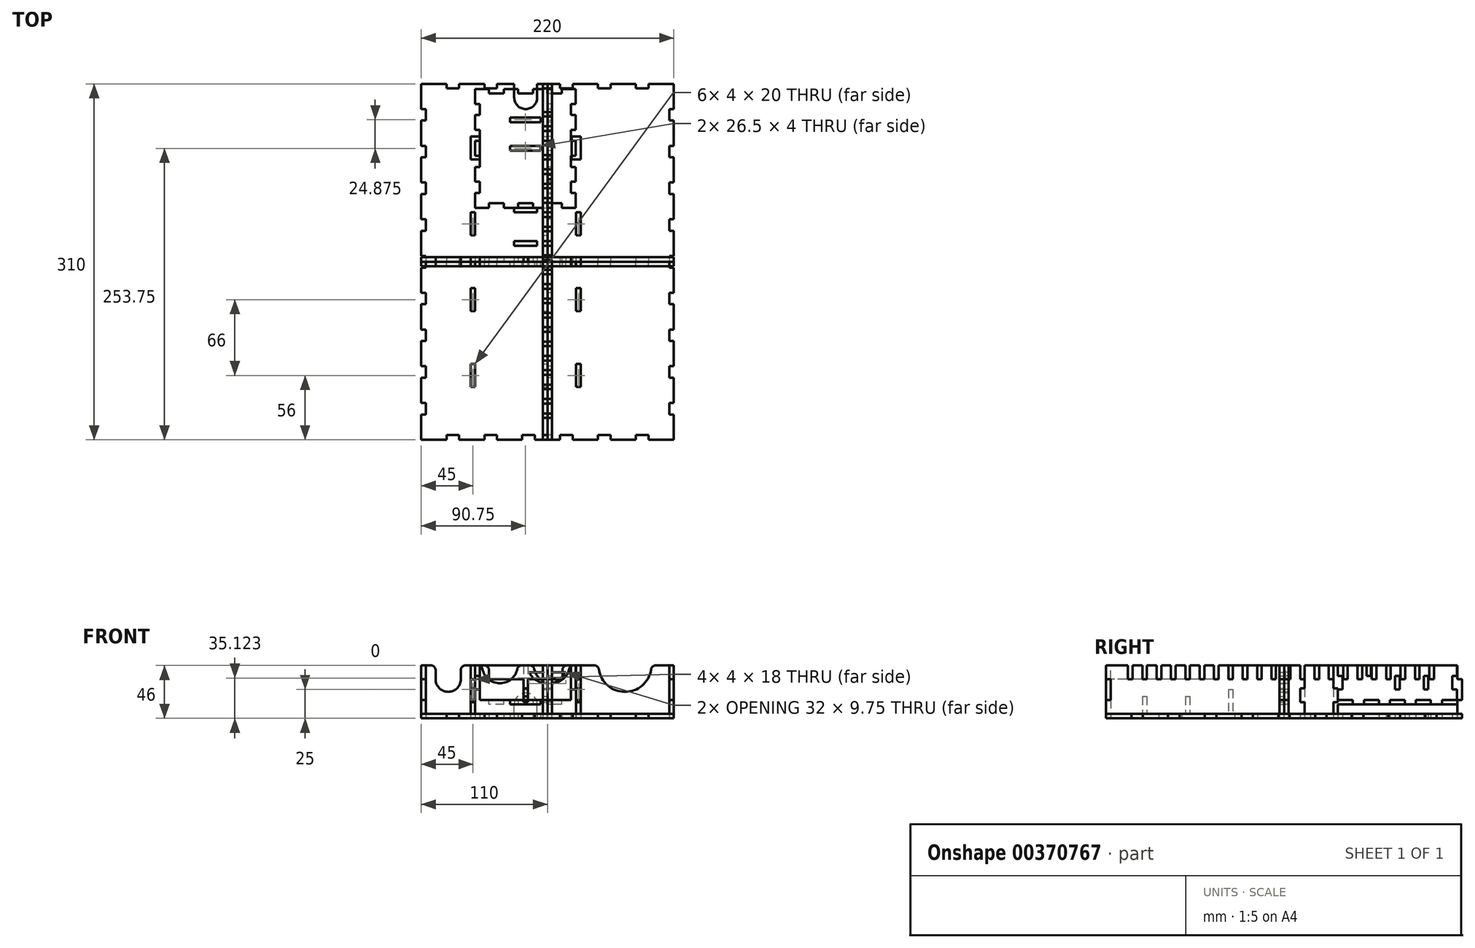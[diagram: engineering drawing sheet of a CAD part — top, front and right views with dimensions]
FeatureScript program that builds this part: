
annotation { "Feature Type Name" : "Feature", "Feature Type Description" : "" }
export const myFeature = defineFeature(function(context is Context, id is Id, definition is map)
    precondition{}
    {
        {
            assignVariable(context, id + "F0", {"name" : "thickness", "anyValue" : 4});
        }
        {
            var Q0;
            Q0=qCreatedBy(makeId("Top.planeOp"),FACE);
            var sketch = newSketch(context, id + "F1", { "sketchPlane" : qUnion([Q0])});
            skLineSegment(sketch, "E0", {"start": v(-110, 155) * mm, "end": v(-110, 133) * mm});
            skLineSegment(sketch, "E1", {"start": v(-110, 133) * mm, "end": v(-106, 133) * mm});
            skLineSegment(sketch, "E2", {"start": v(-106, 133) * mm, "end": v(-106, 123) * mm});
            skLineSegment(sketch, "E3", {"start": v(-106, 123) * mm, "end": v(-110, 123) * mm});
            skLineSegment(sketch, "E4.0.1.0", {"start": v(-106, 91) * mm, "end": v(-110, 91) * mm});
            skLineSegment(sketch, "E4.0.1.1", {"start": v(-110, 123) * mm, "end": v(-110, 101) * mm});
            skLineSegment(sketch, "E4.0.1.2", {"start": v(-106, 101) * mm, "end": v(-106, 91) * mm});
            skLineSegment(sketch, "E4.0.1.3", {"start": v(-110, 101) * mm, "end": v(-106, 101) * mm});
            skLineSegment(sketch, "E4.0.2.0", {"start": v(-106, 59) * mm, "end": v(-110, 59) * mm});
            skLineSegment(sketch, "E4.0.2.1", {"start": v(-110, 91) * mm, "end": v(-110, 69) * mm});
            skLineSegment(sketch, "E4.0.2.2", {"start": v(-106, 69) * mm, "end": v(-106, 59) * mm});
            skLineSegment(sketch, "E4.0.2.3", {"start": v(-110, 69) * mm, "end": v(-106, 69) * mm});
            skLineSegment(sketch, "E4.0.3.0", {"start": v(-106, 27) * mm, "end": v(-110, 27) * mm});
            skLineSegment(sketch, "E4.0.3.1", {"start": v(-110, 59) * mm, "end": v(-110, 37) * mm});
            skLineSegment(sketch, "E4.0.3.2", {"start": v(-106, 37) * mm, "end": v(-106, 27) * mm});
            skLineSegment(sketch, "E4.0.3.3", {"start": v(-110, 37) * mm, "end": v(-106, 37) * mm});
            skLineSegment(sketch, "E4.0.4.0", {"start": v(-106, -5) * mm, "end": v(-110, -5) * mm});
            skLineSegment(sketch, "E4.0.4.1", {"start": v(-110, 27) * mm, "end": v(-110, 5) * mm});
            skLineSegment(sketch, "E4.0.4.2", {"start": v(-106, 5) * mm, "end": v(-106, -5) * mm});
            skLineSegment(sketch, "E4.0.4.3", {"start": v(-110, 5) * mm, "end": v(-106, 5) * mm});
            skLineSegment(sketch, "E4.0.5.0", {"start": v(-106, -37) * mm, "end": v(-110, -37) * mm});
            skLineSegment(sketch, "E4.0.5.1", {"start": v(-110, -5) * mm, "end": v(-110, -27) * mm});
            skLineSegment(sketch, "E4.0.5.2", {"start": v(-106, -27) * mm, "end": v(-106, -37) * mm});
            skLineSegment(sketch, "E4.0.5.3", {"start": v(-110, -27) * mm, "end": v(-106, -27) * mm});
            skLineSegment(sketch, "E4.0.6.0", {"start": v(-106, -69) * mm, "end": v(-110, -69) * mm});
            skLineSegment(sketch, "E4.0.6.1", {"start": v(-110, -37) * mm, "end": v(-110, -59) * mm});
            skLineSegment(sketch, "E4.0.6.2", {"start": v(-106, -59) * mm, "end": v(-106, -69) * mm});
            skLineSegment(sketch, "E4.0.6.3", {"start": v(-110, -59) * mm, "end": v(-106, -59) * mm});
            skLineSegment(sketch, "E4.0.7.0", {"start": v(-106, -101) * mm, "end": v(-110, -101) * mm});
            skLineSegment(sketch, "E4.0.7.1", {"start": v(-110, -69) * mm, "end": v(-110, -91) * mm});
            skLineSegment(sketch, "E4.0.7.2", {"start": v(-106, -91) * mm, "end": v(-106, -101) * mm});
            skLineSegment(sketch, "E4.0.7.3", {"start": v(-110, -91) * mm, "end": v(-106, -91) * mm});
            skLineSegment(sketch, "E4.0.8.0", {"start": v(-106, -133) * mm, "end": v(-110, -133) * mm});
            skLineSegment(sketch, "E4.0.8.1", {"start": v(-110, -101) * mm, "end": v(-110, -123) * mm});
            skLineSegment(sketch, "E4.0.8.2", {"start": v(-106, -123) * mm, "end": v(-106, -133) * mm});
            skLineSegment(sketch, "E4.0.8.3", {"start": v(-110, -123) * mm, "end": v(-106, -123) * mm});
            skLineSegment(sketch, "E4.0.9.1", {"start": v(-110, -133) * mm, "end": v(-110, -155) * mm});
            skLineSegment(sketch, "E5", {"start": v(-110, 155) * mm, "end": v(-88, 155) * mm});
            skLineSegment(sketch, "E6", {"start": v(-88, 155) * mm, "end": v(-88, 151) * mm});
            skLineSegment(sketch, "E7", {"start": v(-88, 151) * mm, "end": v(-77, 151) * mm});
            skLineSegment(sketch, "E8", {"start": v(-77, 151) * mm, "end": v(-77, 155) * mm});
            skLineSegment(sketch, "E9.1.0.0", {"start": v(-44, 151) * mm, "end": v(-44, 155) * mm});
            skLineSegment(sketch, "E9.1.0.1", {"start": v(-55, 151) * mm, "end": v(-44, 151) * mm});
            skLineSegment(sketch, "E9.1.0.2", {"start": v(-77, 155) * mm, "end": v(-55, 155) * mm});
            skLineSegment(sketch, "E9.1.0.3", {"start": v(-55, 155) * mm, "end": v(-55, 151) * mm});
            skLineSegment(sketch, "E9.2.0.0", {"start": v(-11, 151) * mm, "end": v(-11, 155) * mm, "construction": true});
            skLineSegment(sketch, "E9.2.0.1", {"start": v(-22, 151) * mm, "end": v(-11, 151) * mm, "construction": true});
            skLineSegment(sketch, "E9.2.0.2", {"start": v(-44, 155) * mm, "end": v(-22, 155) * mm, "construction": true});
            skLineSegment(sketch, "E9.2.0.3", {"start": v(-22, 155) * mm, "end": v(-22, 151) * mm, "construction": true});
            skLineSegment(sketch, "E9.3.0.0", {"start": v(22, 151) * mm, "end": v(22, 155) * mm});
            skLineSegment(sketch, "E9.3.0.1", {"start": v(11, 151) * mm, "end": v(22, 151) * mm});
            skLineSegment(sketch, "E9.3.0.2", {"start": v(-11, 155) * mm, "end": v(11, 155) * mm, "construction": true});
            skLineSegment(sketch, "E9.3.0.3", {"start": v(11, 155) * mm, "end": v(11, 151) * mm});
            skLineSegment(sketch, "E9.4.0.0", {"start": v(55, 151) * mm, "end": v(55, 155) * mm});
            skLineSegment(sketch, "E9.4.0.1", {"start": v(44, 151) * mm, "end": v(55, 151) * mm});
            skLineSegment(sketch, "E9.4.0.2", {"start": v(22, 155) * mm, "end": v(44, 155) * mm});
            skLineSegment(sketch, "E9.4.0.3", {"start": v(44, 155) * mm, "end": v(44, 151) * mm});
            skLineSegment(sketch, "E9.5.0.0", {"start": v(88, 151) * mm, "end": v(88, 155) * mm});
            skLineSegment(sketch, "E9.5.0.1", {"start": v(77, 151) * mm, "end": v(88, 151) * mm});
            skLineSegment(sketch, "E9.5.0.2", {"start": v(55, 155) * mm, "end": v(77, 155) * mm});
            skLineSegment(sketch, "E9.5.0.3", {"start": v(77, 155) * mm, "end": v(77, 151) * mm});
            skLineSegment(sketch, "E9.6.0.2", {"start": v(88, 155) * mm, "end": v(110, 155) * mm});
            skPoint(sketch, "E10.endSnap0", {"position": v(-106, 0) * mm});
            skLineSegment(sketch, "E11.MirrorCS", {"start": v(106, -37) * mm, "end": v(110, -37) * mm});
            skLineSegment(sketch, "E12.MirrorCS", {"start": v(106, -27) * mm, "end": v(106, -37) * mm});
            skLineSegment(sketch, "E13.MirrorCS", {"start": v(106, -5) * mm, "end": v(110, -5) * mm});
            skLineSegment(sketch, "E14.MirrorCS", {"start": v(110, -133) * mm, "end": v(110, -155) * mm});
            skLineSegment(sketch, "E15.MirrorCS", {"start": v(106, 133) * mm, "end": v(106, 123) * mm});
            skLineSegment(sketch, "E16.MirrorCS", {"start": v(110, -59) * mm, "end": v(106, -59) * mm});
            skLineSegment(sketch, "E17.MirrorCS", {"start": v(110, -123) * mm, "end": v(106, -123) * mm});
            skLineSegment(sketch, "E18.MirrorCS", {"start": v(106, -91) * mm, "end": v(106, -101) * mm});
            skLineSegment(sketch, "E19.MirrorCS", {"start": v(106, -133) * mm, "end": v(110, -133) * mm});
            skLineSegment(sketch, "E20.MirrorCS", {"start": v(110, 69) * mm, "end": v(106, 69) * mm});
            skLineSegment(sketch, "E21.MirrorCS", {"start": v(106, 27) * mm, "end": v(110, 27) * mm});
            skLineSegment(sketch, "E22.MirrorCS", {"start": v(106, -101) * mm, "end": v(110, -101) * mm});
            skLineSegment(sketch, "E23.MirrorCS", {"start": v(110, -5) * mm, "end": v(110, -27) * mm});
            skLineSegment(sketch, "E24.MirrorCS", {"start": v(106, -59) * mm, "end": v(106, -69) * mm});
            skLineSegment(sketch, "E25.MirrorCS", {"start": v(106, 37) * mm, "end": v(106, 27) * mm});
            skLineSegment(sketch, "E26.MirrorCS", {"start": v(110, 133) * mm, "end": v(106, 133) * mm});
            skLineSegment(sketch, "E27.MirrorCS", {"start": v(106, 69) * mm, "end": v(106, 59) * mm});
            skLineSegment(sketch, "E28.MirrorCS", {"start": v(106, 59) * mm, "end": v(110, 59) * mm});
            skLineSegment(sketch, "E29.MirrorCS", {"start": v(110, 37) * mm, "end": v(106, 37) * mm});
            skLineSegment(sketch, "E30.MirrorCS", {"start": v(106, -69) * mm, "end": v(110, -69) * mm});
            skLineSegment(sketch, "E31.MirrorCS", {"start": v(106, 91) * mm, "end": v(110, 91) * mm});
            skLineSegment(sketch, "E32.MirrorCS", {"start": v(106, 101) * mm, "end": v(106, 91) * mm});
            skLineSegment(sketch, "E33.MirrorCS", {"start": v(110, 27) * mm, "end": v(110, 5) * mm});
            skLineSegment(sketch, "E34.MirrorCS", {"start": v(110, 5) * mm, "end": v(106, 5) * mm});
            skLineSegment(sketch, "E35.MirrorCS", {"start": v(110, 155) * mm, "end": v(110, 133) * mm});
            skLineSegment(sketch, "E36.MirrorCS", {"start": v(110, -101) * mm, "end": v(110, -123) * mm});
            skLineSegment(sketch, "E37.MirrorCS", {"start": v(106, 123) * mm, "end": v(110, 123) * mm});
            skLineSegment(sketch, "E38.MirrorCS", {"start": v(110, -27) * mm, "end": v(106, -27) * mm});
            skLineSegment(sketch, "E39.MirrorCS", {"start": v(106, -123) * mm, "end": v(106, -133) * mm});
            skLineSegment(sketch, "E40.MirrorCS", {"start": v(110, -91) * mm, "end": v(106, -91) * mm});
            skLineSegment(sketch, "E41.MirrorCS", {"start": v(106, 5) * mm, "end": v(106, -5) * mm});
            skLineSegment(sketch, "E42.MirrorCS", {"start": v(110, 101) * mm, "end": v(106, 101) * mm});
            skLineSegment(sketch, "E43.MirrorCS", {"start": v(110, 59) * mm, "end": v(110, 37) * mm});
            skLineSegment(sketch, "E44.MirrorCS", {"start": v(110, -69) * mm, "end": v(110, -91) * mm});
            skLineSegment(sketch, "E45.MirrorCS", {"start": v(110, 91) * mm, "end": v(110, 69) * mm});
            skLineSegment(sketch, "E46.MirrorCS", {"start": v(110, -37) * mm, "end": v(110, -59) * mm});
            skLineSegment(sketch, "E47.MirrorCS", {"start": v(110, 123) * mm, "end": v(110, 101) * mm});
            skLineSegment(sketch, "E48.MirrorCS", {"start": v(-11, -151) * mm, "end": v(-11, -155) * mm});
            skLineSegment(sketch, "E49.MirrorCS", {"start": v(22, -155) * mm, "end": v(44, -155) * mm});
            skLineSegment(sketch, "E50.MirrorCS", {"start": v(-55, -151) * mm, "end": v(-44, -151) * mm});
            skLineSegment(sketch, "E51.MirrorCS", {"start": v(-44, -151) * mm, "end": v(-44, -155) * mm});
            skLineSegment(sketch, "E52.MirrorCS", {"start": v(11, -151) * mm, "end": v(22, -151) * mm});
            skLineSegment(sketch, "E53.MirrorCS", {"start": v(22, -151) * mm, "end": v(22, -155) * mm});
            skLineSegment(sketch, "E54.MirrorCS", {"start": v(-22, -151) * mm, "end": v(-11, -151) * mm});
            skLineSegment(sketch, "E55.MirrorCS", {"start": v(77, -151) * mm, "end": v(88, -151) * mm});
            skLineSegment(sketch, "E56.MirrorCS", {"start": v(-11, -155) * mm, "end": v(11, -155) * mm});
            skLineSegment(sketch, "E57.MirrorCS", {"start": v(-77, -155) * mm, "end": v(-55, -155) * mm});
            skLineSegment(sketch, "E58.MirrorCS", {"start": v(-88, -155) * mm, "end": v(-88, -151) * mm});
            skLineSegment(sketch, "E59.MirrorCS", {"start": v(-22, -155) * mm, "end": v(-22, -151) * mm});
            skLineSegment(sketch, "E60.MirrorCS", {"start": v(44, -155) * mm, "end": v(44, -151) * mm});
            skLineSegment(sketch, "E61.MirrorCS", {"start": v(44, -151) * mm, "end": v(55, -151) * mm});
            skLineSegment(sketch, "E62.MirrorCS", {"start": v(-77, -151) * mm, "end": v(-77, -155) * mm});
            skLineSegment(sketch, "E63.MirrorCS", {"start": v(77, -155) * mm, "end": v(77, -151) * mm});
            skLineSegment(sketch, "E64.MirrorCS", {"start": v(88, -155) * mm, "end": v(110, -155) * mm});
            skLineSegment(sketch, "E65.MirrorCS", {"start": v(-110, -155) * mm, "end": v(-88, -155) * mm});
            skLineSegment(sketch, "E66.MirrorCS", {"start": v(11, -155) * mm, "end": v(11, -151) * mm});
            skLineSegment(sketch, "E67.MirrorCS", {"start": v(-55, -155) * mm, "end": v(-55, -151) * mm});
            skLineSegment(sketch, "E68.MirrorCS", {"start": v(55, -151) * mm, "end": v(55, -155) * mm});
            skLineSegment(sketch, "E69.MirrorCS", {"start": v(88, -151) * mm, "end": v(88, -155) * mm});
            skLineSegment(sketch, "E70.MirrorCS", {"start": v(-88, -151) * mm, "end": v(-77, -151) * mm});
            skLineSegment(sketch, "E71.MirrorCS", {"start": v(55, -155) * mm, "end": v(77, -155) * mm});
            skLineSegment(sketch, "E72.MirrorCS", {"start": v(-44, -155) * mm, "end": v(-22, -155) * mm});
            skLineSegment(sketch, "E73", {"start": v(-65, 163.65) * mm, "end": v(-65, -222.9) * mm, "construction": true});
            skLineSegment(sketch, "E74", {"start": v(-19, 166.4) * mm, "end": v(-19, -214.65) * mm, "construction": true});
            skLineSegment(sketch, "E75", {"start": v(27, 161.08) * mm, "end": v(27, -222.02) * mm, "construction": true});
            skLineSegment(sketch, "E76", {"start": v(-29, 155) * mm, "end": v(-29, 143) * mm});
            skLineSegment(sketch, "E77", {"start": v(-9, 155) * mm, "end": v(-9, 143) * mm});
            skArc(sketch, "E78", {"start": v(-29, 143) * mm, "mid": v(-19, 133) * mm, "end": v(-9, 143) * mm});
            skLineSegment(sketch, "E79", {"start": v(-44, 155) * mm, "end": v(-29, 155) * mm});
            skLineSegment(sketch, "E80", {"start": v(-9, 155) * mm, "end": v(11, 155) * mm});
            skLineSegment(sketch, "E81.bottom", {"start": v(21, 109) * mm, "end": v(29, 109) * mm});
            skLineSegment(sketch, "E81.top", {"start": v(21, 89) * mm, "end": v(29, 89) * mm});
            skLineSegment(sketch, "E81.left", {"start": v(21, 109) * mm, "end": v(21, 89) * mm});
            skLineSegment(sketch, "E81.right", {"start": v(29, 109) * mm, "end": v(29, 89) * mm});
            skLineSegment(sketch, "E82.bottom", {"start": v(25, 43) * mm, "end": v(29, 43) * mm});
            skLineSegment(sketch, "E82.top", {"start": v(25, 23) * mm, "end": v(29, 23) * mm});
            skLineSegment(sketch, "E82.left", {"start": v(25, 43) * mm, "end": v(25, 23) * mm});
            skLineSegment(sketch, "E82.right", {"start": v(29, 43) * mm, "end": v(29, 23) * mm});
            skLineSegment(sketch, "E83.bottom", {"start": v(25, -23) * mm, "end": v(29, -23) * mm});
            skLineSegment(sketch, "E83.top", {"start": v(25, -43) * mm, "end": v(29, -43) * mm});
            skLineSegment(sketch, "E83.left", {"start": v(25, -23) * mm, "end": v(25, -43) * mm});
            skLineSegment(sketch, "E83.right", {"start": v(29, -23) * mm, "end": v(29, -43) * mm});
            skLineSegment(sketch, "E84.bottom", {"start": v(25, -89) * mm, "end": v(29, -89) * mm});
            skLineSegment(sketch, "E84.top", {"start": v(25, -109) * mm, "end": v(29, -109) * mm});
            skLineSegment(sketch, "E84.left", {"start": v(25, -89) * mm, "end": v(25, -109) * mm});
            skLineSegment(sketch, "E84.right", {"start": v(29, -89) * mm, "end": v(29, -109) * mm});
            skLineSegment(sketch, "E85", {"start": v(29, 109) * mm, "end": v(29, 155) * mm, "construction": true});
            skPoint(sketch, "E85.endSnap0", {"position": v(33, 155) * mm});
            skLineSegment(sketch, "E86", {"start": v(29, 89) * mm, "end": v(29, 43) * mm, "construction": true});
            skLineSegment(sketch, "E87", {"start": v(29, 23) * mm, "end": v(29, -23) * mm, "construction": true});
            skLineSegment(sketch, "E88", {"start": v(29, -43) * mm, "end": v(29, -89) * mm, "construction": true});
            skLineSegment(sketch, "E89", {"start": v(29, -109) * mm, "end": v(29, -155) * mm, "construction": true});
            skLineSegment(sketch, "E90.MirrorCS", {"start": v(-63, -109) * mm, "end": v(-67, -109) * mm});
            skLineSegment(sketch, "E91.MirrorCS", {"start": v(-59, 109) * mm, "end": v(-67, 109) * mm});
            skLineSegment(sketch, "E92.MirrorCS", {"start": v(-63, 43) * mm, "end": v(-67, 43) * mm});
            skLineSegment(sketch, "E93.MirrorCS", {"start": v(-59, 89) * mm, "end": v(-67, 89) * mm});
            skLineSegment(sketch, "E94.MirrorCS", {"start": v(-63, -23) * mm, "end": v(-67, -23) * mm});
            skLineSegment(sketch, "E95.MirrorCS", {"start": v(-63, 23) * mm, "end": v(-67, 23) * mm});
            skLineSegment(sketch, "E96.MirrorCS", {"start": v(-63, -89) * mm, "end": v(-67, -89) * mm});
            skLineSegment(sketch, "E97.MirrorCS", {"start": v(-63, -43) * mm, "end": v(-67, -43) * mm});
            skLineSegment(sketch, "E98.MirrorCS", {"start": v(-67, -89) * mm, "end": v(-67, -109) * mm});
            skLineSegment(sketch, "E99.MirrorCS", {"start": v(-67, -23) * mm, "end": v(-67, -43) * mm});
            skLineSegment(sketch, "E100.MirrorCS", {"start": v(-59, 109) * mm, "end": v(-59, 89) * mm});
            skLineSegment(sketch, "E101.MirrorCS", {"start": v(-63, 43) * mm, "end": v(-63, 23) * mm});
            skLineSegment(sketch, "E102.MirrorCS", {"start": v(-67, 109) * mm, "end": v(-67, 89) * mm});
            skLineSegment(sketch, "E103.MirrorCS", {"start": v(-67, 43) * mm, "end": v(-67, 23) * mm});
            skLineSegment(sketch, "E104.MirrorCS", {"start": v(-63, -89) * mm, "end": v(-63, -109) * mm});
            skLineSegment(sketch, "E105.MirrorCS", {"start": v(-63, -23) * mm, "end": v(-63, -43) * mm});
            skLineSegment(sketch, "E106", {"start": v(-151.25, 45) * mm, "end": v(136.26, 45) * mm, "construction": true});
            skLineSegment(sketch, "E107", {"start": v(137.08, 16) * mm, "end": v(-152.07, 16) * mm, "construction": true});
            skLineSegment(sketch, "E108.bottom", {"start": v(-29, 47) * mm, "end": v(-9, 47) * mm});
            skLineSegment(sketch, "E108.top", {"start": v(-29, 43) * mm, "end": v(-9, 43) * mm});
            skLineSegment(sketch, "E108.left", {"start": v(-29, 47) * mm, "end": v(-29, 43) * mm});
            skLineSegment(sketch, "E108.right", {"start": v(-9, 47) * mm, "end": v(-9, 43) * mm});
            skLineSegment(sketch, "E109.bottom", {"start": v(-29, 18) * mm, "end": v(-9, 18) * mm});
            skLineSegment(sketch, "E109.top", {"start": v(-29, 14) * mm, "end": v(-9, 14) * mm});
            skLineSegment(sketch, "E109.left", {"start": v(-29, 18) * mm, "end": v(-29, 14) * mm});
            skLineSegment(sketch, "E109.right", {"start": v(-9, 18) * mm, "end": v(-9, 14) * mm});
            skSolve(sketch);
        }
        {
            var Q0;
            Q0 = qSketchRegion(id + "F1", true);
            extrude(context, id + "F2", {"entities" : qUnion([Q0]), "depth" : 4 * mm});
        }
        {
            var Q0;
            Q0=qCreatedBy(makeId("Right.planeOp"),FACE);
            var sketch = newSketch(context, id + "F3", { "sketchPlane" : qUnion([Q0])});
            skLineSegment(sketch, "E110.top", {"start": v(-151, 4) * mm, "end": v(151, 4) * mm});
            skLineSegment(sketch, "E111.bottom", {"start": v(-151, 34) * mm, "end": v(-155, 34) * mm});
            skLineSegment(sketch, "E111.top", {"start": v(-151, 16) * mm, "end": v(-155, 16) * mm});
            skPoint(sketch, "E112.oppositeSnap0", {"position": v(-153, 16) * mm});
            skLineSegment(sketch, "E112.bottom", {"start": v(155, 34) * mm, "end": v(151, 34) * mm});
            skLineSegment(sketch, "E112.top", {"start": v(155, 16) * mm, "end": v(151, 16) * mm});
            skLineSegment(sketch, "E113.bottom", {"start": v(-133, 0) * mm, "end": v(-123, 0) * mm});
            skLineSegment(sketch, "E113.top", {"start": v(-133, 4) * mm, "end": v(-123, 4) * mm});
            skLineSegment(sketch, "E113.left", {"start": v(-133, 0) * mm, "end": v(-133, 4) * mm});
            skLineSegment(sketch, "E113.right", {"start": v(-123, 0) * mm, "end": v(-123, 4) * mm});
            skLineSegment(sketch, "E114.1.0.0", {"start": v(-101, 4) * mm, "end": v(-91, 4) * mm});
            skLineSegment(sketch, "E114.1.0.1", {"start": v(-101, 0) * mm, "end": v(-101, 4) * mm});
            skLineSegment(sketch, "E114.1.0.2", {"start": v(-91, 0) * mm, "end": v(-91, 4) * mm});
            skLineSegment(sketch, "E114.1.0.3", {"start": v(-101, 0) * mm, "end": v(-91, 0) * mm});
            skLineSegment(sketch, "E114.2.0.0", {"start": v(-69, 4) * mm, "end": v(-59, 4) * mm});
            skLineSegment(sketch, "E114.2.0.1", {"start": v(-69, 0) * mm, "end": v(-69, 4) * mm});
            skLineSegment(sketch, "E114.2.0.2", {"start": v(-59, 0) * mm, "end": v(-59, 4) * mm});
            skLineSegment(sketch, "E114.2.0.3", {"start": v(-69, 0) * mm, "end": v(-59, 0) * mm});
            skLineSegment(sketch, "E114.3.0.0", {"start": v(-37, 4) * mm, "end": v(-27, 4) * mm});
            skLineSegment(sketch, "E114.3.0.1", {"start": v(-37, 0) * mm, "end": v(-37, 4) * mm});
            skLineSegment(sketch, "E114.3.0.2", {"start": v(-27, 0) * mm, "end": v(-27, 4) * mm});
            skLineSegment(sketch, "E114.3.0.3", {"start": v(-37, 0) * mm, "end": v(-27, 0) * mm});
            skLineSegment(sketch, "E114.4.0.0", {"start": v(-5, 4) * mm, "end": v(5, 4) * mm});
            skLineSegment(sketch, "E114.4.0.1", {"start": v(-5, 0) * mm, "end": v(-5, 4) * mm});
            skLineSegment(sketch, "E114.4.0.2", {"start": v(5, 0) * mm, "end": v(5, 4) * mm});
            skLineSegment(sketch, "E114.4.0.3", {"start": v(-5, 0) * mm, "end": v(5, 0) * mm});
            skLineSegment(sketch, "E114.5.0.0", {"start": v(27, 4) * mm, "end": v(37, 4) * mm});
            skLineSegment(sketch, "E114.5.0.1", {"start": v(27, 0) * mm, "end": v(27, 4) * mm});
            skLineSegment(sketch, "E114.5.0.2", {"start": v(37, 0) * mm, "end": v(37, 4) * mm});
            skLineSegment(sketch, "E114.5.0.3", {"start": v(27, 0) * mm, "end": v(37, 0) * mm});
            skLineSegment(sketch, "E114.6.0.0", {"start": v(59, 4) * mm, "end": v(69, 4) * mm});
            skLineSegment(sketch, "E114.6.0.1", {"start": v(59, 0) * mm, "end": v(59, 4) * mm});
            skLineSegment(sketch, "E114.6.0.2", {"start": v(69, 0) * mm, "end": v(69, 4) * mm});
            skLineSegment(sketch, "E114.6.0.3", {"start": v(59, 0) * mm, "end": v(69, 0) * mm});
            skLineSegment(sketch, "E114.7.0.0", {"start": v(91, 4) * mm, "end": v(101, 4) * mm});
            skLineSegment(sketch, "E114.7.0.1", {"start": v(91, 0) * mm, "end": v(91, 4) * mm});
            skLineSegment(sketch, "E114.7.0.2", {"start": v(101, 0) * mm, "end": v(101, 4) * mm});
            skLineSegment(sketch, "E114.7.0.3", {"start": v(91, 0) * mm, "end": v(101, 0) * mm});
            skLineSegment(sketch, "E114.8.0.0", {"start": v(123, 4) * mm, "end": v(133, 4) * mm});
            skLineSegment(sketch, "E114.8.0.1", {"start": v(123, 0) * mm, "end": v(123, 4) * mm});
            skLineSegment(sketch, "E114.8.0.2", {"start": v(133, 0) * mm, "end": v(133, 4) * mm});
            skLineSegment(sketch, "E114.8.0.3", {"start": v(123, 0) * mm, "end": v(133, 0) * mm});
            skLineSegment(sketch, "E114.direction1", {"start": v(-133, 0) * mm, "end": v(-101, 0) * mm, "construction": true});
            skLineSegment(sketch, "E115.top", {"start": v(-151, 46) * mm, "end": v(-136, 46) * mm});
            skLineSegment(sketch, "E115.right", {"start": v(-136, 34) * mm, "end": v(-136, 46) * mm});
            skLineSegment(sketch, "E116.top", {"start": v(151, 46) * mm, "end": v(130.5, 46) * mm});
            skLineSegment(sketch, "E116.right", {"start": v(130.5, 34) * mm, "end": v(130.5, 46) * mm});
            skLineSegment(sketch, "E117.top", {"start": v(-132, 46) * mm, "end": v(-123.5, 46) * mm});
            skLineSegment(sketch, "E117.left", {"start": v(-132, 34) * mm, "end": v(-132, 46) * mm});
            skLineSegment(sketch, "E117.right", {"start": v(-123.5, 34) * mm, "end": v(-123.5, 46) * mm});
            skLineSegment(sketch, "E118", {"start": v(-136, 34) * mm, "end": v(-132, 34) * mm});
            skLineSegment(sketch, "E119", {"start": v(130.5, 34) * mm, "end": v(126.5, 34) * mm});
            skLineSegment(sketch, "E120.1.0.0", {"start": v(-123.5, 34) * mm, "end": v(-119.5, 34) * mm});
            skLineSegment(sketch, "E120.1.0.1", {"start": v(-111, 34) * mm, "end": v(-111, 46) * mm});
            skLineSegment(sketch, "E120.1.0.2", {"start": v(-119.5, 46) * mm, "end": v(-111, 46) * mm});
            skLineSegment(sketch, "E120.1.0.3", {"start": v(-119.5, 34) * mm, "end": v(-119.5, 46) * mm});
            skLineSegment(sketch, "E120.2.0.0", {"start": v(-111, 34) * mm, "end": v(-107, 34) * mm});
            skLineSegment(sketch, "E120.2.0.1", {"start": v(-98.5, 34) * mm, "end": v(-98.5, 46) * mm});
            skLineSegment(sketch, "E120.2.0.2", {"start": v(-107, 46) * mm, "end": v(-98.5, 46) * mm});
            skLineSegment(sketch, "E120.2.0.3", {"start": v(-107, 34) * mm, "end": v(-107, 46) * mm});
            skLineSegment(sketch, "E120.3.0.0", {"start": v(-98.5, 34) * mm, "end": v(-94.5, 34) * mm});
            skLineSegment(sketch, "E120.3.0.1", {"start": v(-86, 34) * mm, "end": v(-86, 46) * mm});
            skLineSegment(sketch, "E120.3.0.2", {"start": v(-94.5, 46) * mm, "end": v(-86, 46) * mm});
            skLineSegment(sketch, "E120.3.0.3", {"start": v(-94.5, 34) * mm, "end": v(-94.5, 46) * mm});
            skLineSegment(sketch, "E120.4.0.0", {"start": v(-86, 34) * mm, "end": v(-82, 34) * mm});
            skLineSegment(sketch, "E120.4.0.1", {"start": v(-73.5, 34) * mm, "end": v(-73.5, 46) * mm});
            skLineSegment(sketch, "E120.4.0.2", {"start": v(-82, 46) * mm, "end": v(-73.5, 46) * mm});
            skLineSegment(sketch, "E120.4.0.3", {"start": v(-82, 34) * mm, "end": v(-82, 46) * mm});
            skLineSegment(sketch, "E120.5.0.0", {"start": v(-73.5, 34) * mm, "end": v(-69.5, 34) * mm});
            skLineSegment(sketch, "E120.5.0.1", {"start": v(-61, 34) * mm, "end": v(-61, 46) * mm});
            skLineSegment(sketch, "E120.5.0.2", {"start": v(-69.5, 46) * mm, "end": v(-61, 46) * mm});
            skLineSegment(sketch, "E120.5.0.3", {"start": v(-69.5, 34) * mm, "end": v(-69.5, 46) * mm});
            skLineSegment(sketch, "E120.6.0.0", {"start": v(-61, 34) * mm, "end": v(-57, 34) * mm});
            skLineSegment(sketch, "E120.6.0.1", {"start": v(-48.5, 34) * mm, "end": v(-48.5, 46) * mm});
            skLineSegment(sketch, "E120.6.0.2", {"start": v(-57, 46) * mm, "end": v(-48.5, 46) * mm});
            skLineSegment(sketch, "E120.6.0.3", {"start": v(-57, 34) * mm, "end": v(-57, 46) * mm});
            skLineSegment(sketch, "E120.7.0.0", {"start": v(-48.5, 34) * mm, "end": v(-44.5, 34) * mm});
            skLineSegment(sketch, "E120.7.0.1", {"start": v(-36, 34) * mm, "end": v(-36, 46) * mm});
            skLineSegment(sketch, "E120.7.0.2", {"start": v(-44.5, 46) * mm, "end": v(-36, 46) * mm});
            skLineSegment(sketch, "E120.7.0.3", {"start": v(-44.5, 34) * mm, "end": v(-44.5, 46) * mm});
            skLineSegment(sketch, "E120.8.0.0", {"start": v(-36, 34) * mm, "end": v(-32, 34) * mm});
            skLineSegment(sketch, "E120.8.0.1", {"start": v(-23.5, 34) * mm, "end": v(-23.5, 46) * mm});
            skLineSegment(sketch, "E120.8.0.2", {"start": v(-32, 46) * mm, "end": v(-23.5, 46) * mm});
            skLineSegment(sketch, "E120.8.0.3", {"start": v(-32, 34) * mm, "end": v(-32, 46) * mm});
            skLineSegment(sketch, "E120.9.0.0", {"start": v(-23.5, 34) * mm, "end": v(-19.5, 34) * mm});
            skLineSegment(sketch, "E120.9.0.1", {"start": v(-11, 34) * mm, "end": v(-11, 46) * mm});
            skLineSegment(sketch, "E120.9.0.2", {"start": v(-19.5, 46) * mm, "end": v(-11, 46) * mm});
            skLineSegment(sketch, "E120.9.0.3", {"start": v(-19.5, 34) * mm, "end": v(-19.5, 46) * mm});
            skLineSegment(sketch, "E120.10.0.0", {"start": v(-11, 34) * mm, "end": v(-7, 34) * mm});
            skLineSegment(sketch, "E120.10.0.1", {"start": v(1.5, 34) * mm, "end": v(1.5, 46) * mm});
            skLineSegment(sketch, "E120.10.0.2", {"start": v(-7, 46) * mm, "end": v(1.5, 46) * mm});
            skLineSegment(sketch, "E120.10.0.3", {"start": v(-7, 34) * mm, "end": v(-7, 46) * mm});
            skLineSegment(sketch, "E120.11.0.0", {"start": v(1.5, 34) * mm, "end": v(5.5, 34) * mm});
            skLineSegment(sketch, "E120.11.0.1", {"start": v(14, 34) * mm, "end": v(14, 46) * mm});
            skLineSegment(sketch, "E120.11.0.2", {"start": v(5.5, 46) * mm, "end": v(14, 46) * mm});
            skLineSegment(sketch, "E120.11.0.3", {"start": v(5.5, 34) * mm, "end": v(5.5, 46) * mm});
            skLineSegment(sketch, "E120.12.0.0", {"start": v(14, 34) * mm, "end": v(18, 34) * mm});
            skLineSegment(sketch, "E120.12.0.1", {"start": v(26.5, 34) * mm, "end": v(26.5, 46) * mm});
            skLineSegment(sketch, "E120.12.0.2", {"start": v(18, 46) * mm, "end": v(26.5, 46) * mm});
            skLineSegment(sketch, "E120.12.0.3", {"start": v(18, 34) * mm, "end": v(18, 46) * mm});
            skLineSegment(sketch, "E120.13.0.0", {"start": v(26.5, 34) * mm, "end": v(30.5, 34) * mm});
            skLineSegment(sketch, "E120.13.0.1", {"start": v(39, 34) * mm, "end": v(39, 46) * mm});
            skLineSegment(sketch, "E120.13.0.2", {"start": v(30.5, 46) * mm, "end": v(39, 46) * mm});
            skLineSegment(sketch, "E120.13.0.3", {"start": v(30.5, 34) * mm, "end": v(30.5, 46) * mm});
            skLineSegment(sketch, "E120.14.0.0", {"start": v(39, 34) * mm, "end": v(43, 34) * mm});
            skLineSegment(sketch, "E120.14.0.1", {"start": v(51.5, 34) * mm, "end": v(51.5, 46) * mm});
            skLineSegment(sketch, "E120.14.0.2", {"start": v(43, 46) * mm, "end": v(51.5, 46) * mm});
            skLineSegment(sketch, "E120.14.0.3", {"start": v(43, 34) * mm, "end": v(43, 46) * mm});
            skLineSegment(sketch, "E120.15.0.0", {"start": v(51.5, 34) * mm, "end": v(55.5, 34) * mm});
            skLineSegment(sketch, "E120.15.0.1", {"start": v(64, 34) * mm, "end": v(64, 46) * mm});
            skLineSegment(sketch, "E120.15.0.2", {"start": v(55.5, 46) * mm, "end": v(64, 46) * mm});
            skLineSegment(sketch, "E120.15.0.3", {"start": v(55.5, 34) * mm, "end": v(55.5, 46) * mm});
            skLineSegment(sketch, "E120.16.0.0", {"start": v(64, 34) * mm, "end": v(68, 34) * mm});
            skLineSegment(sketch, "E120.16.0.1", {"start": v(76.5, 34) * mm, "end": v(76.5, 46) * mm});
            skLineSegment(sketch, "E120.16.0.2", {"start": v(68, 46) * mm, "end": v(76.5, 46) * mm});
            skLineSegment(sketch, "E120.16.0.3", {"start": v(68, 34) * mm, "end": v(68, 46) * mm});
            skLineSegment(sketch, "E120.17.0.0", {"start": v(76.5, 34) * mm, "end": v(80.5, 34) * mm});
            skLineSegment(sketch, "E120.17.0.1", {"start": v(89, 34) * mm, "end": v(89, 46) * mm});
            skLineSegment(sketch, "E120.17.0.2", {"start": v(80.5, 46) * mm, "end": v(89, 46) * mm});
            skLineSegment(sketch, "E120.17.0.3", {"start": v(80.5, 34) * mm, "end": v(80.5, 46) * mm});
            skLineSegment(sketch, "E120.18.0.0", {"start": v(89, 34) * mm, "end": v(93, 34) * mm});
            skLineSegment(sketch, "E120.18.0.1", {"start": v(101.5, 34) * mm, "end": v(101.5, 46) * mm});
            skLineSegment(sketch, "E120.18.0.2", {"start": v(93, 46) * mm, "end": v(101.5, 46) * mm});
            skLineSegment(sketch, "E120.18.0.3", {"start": v(93, 34) * mm, "end": v(93, 46) * mm});
            skLineSegment(sketch, "E120.19.0.0", {"start": v(101.5, 34) * mm, "end": v(105.5, 34) * mm});
            skLineSegment(sketch, "E120.19.0.1", {"start": v(114, 34) * mm, "end": v(114, 46) * mm});
            skLineSegment(sketch, "E120.19.0.2", {"start": v(105.5, 46) * mm, "end": v(114, 46) * mm});
            skLineSegment(sketch, "E120.19.0.3", {"start": v(105.5, 34) * mm, "end": v(105.5, 46) * mm});
            skLineSegment(sketch, "E120.20.0.0", {"start": v(114, 34) * mm, "end": v(118, 34) * mm});
            skLineSegment(sketch, "E120.20.0.1", {"start": v(126.5, 34) * mm, "end": v(126.5, 46) * mm});
            skLineSegment(sketch, "E120.20.0.2", {"start": v(118, 46) * mm, "end": v(126.5, 46) * mm});
            skLineSegment(sketch, "E120.20.0.3", {"start": v(118, 34) * mm, "end": v(118, 46) * mm});
            skLineSegment(sketch, "E121", {"start": v(18, 84.68) * mm, "end": v(18, -61.22) * mm, "construction": true});
            skLineSegment(sketch, "E122", {"start": v(43, 84.72) * mm, "end": v(43, -60.85) * mm, "construction": true});
            skLineSegment(sketch, "E123", {"start": v(155, 34) * mm, "end": v(155, 16) * mm});
            skLineSegment(sketch, "E124", {"start": v(151, 34) * mm, "end": v(151, 46) * mm});
            skLineSegment(sketch, "E125", {"start": v(151, 16) * mm, "end": v(151, 4) * mm});
            skLineSegment(sketch, "E126", {"start": v(-151, 46) * mm, "end": v(-155, 46) * mm});
            skLineSegment(sketch, "E127", {"start": v(-155, 46) * mm, "end": v(-155, 34) * mm});
            skLineSegment(sketch, "E128", {"start": v(-155, 16) * mm, "end": v(-155, 4) * mm});
            skLineSegment(sketch, "E129", {"start": v(-155, 4) * mm, "end": v(-151, 4) * mm});
            skLineSegment(sketch, "E130", {"start": v(-151, 34) * mm, "end": v(-151, 16) * mm});
            skLineSegment(sketch, "E131", {"start": v(47, -59.92) * mm, "end": v(47, 83.22) * mm, "construction": true});
            skLineSegment(sketch, "E132", {"start": v(14, 85.2) * mm, "end": v(14, -60.46) * mm, "construction": true});
            skSolve(sketch);
        }
        {
            var Q0;
            Q0 = qSketchRegion(id + "F3", true);
            extrude(context, id + "F4", {"entities" : qUnion([Q0]), "depth" : 4 * mm});
        }
        {
            var Q0;
            Q0=qCreatedBy(makeId("Right.planeOp"),FACE);
            var sketch = newSketch(context, id + "F5", { "sketchPlane" : qUnion([Q0])});
            skLineSegment(sketch, "E133.bottom", {"start": v(-151, 34) * mm, "end": v(-155, 34) * mm});
            skLineSegment(sketch, "E133.top", {"start": v(-151, 16) * mm, "end": v(-155, 16) * mm});
            skLineSegment(sketch, "E133.right", {"start": v(-155, 34) * mm, "end": v(-155, 16) * mm});
            skPoint(sketch, "E134.oppositeSnap0", {"position": v(-153, 16) * mm});
            skLineSegment(sketch, "E134.right", {"start": v(155, 34) * mm, "end": v(155, 16) * mm});
            skLineSegment(sketch, "E135", {"start": v(-151, 16) * mm, "end": v(-151, 4) * mm});
            skLineSegment(sketch, "E136.right", {"start": v(-136, 34) * mm, "end": v(-136, 46) * mm});
            skLineSegment(sketch, "E137.right", {"start": v(130.5, 34) * mm, "end": v(130.5, 46) * mm});
            skLineSegment(sketch, "E138.top", {"start": v(-132, 46) * mm, "end": v(-123.5, 46) * mm});
            skLineSegment(sketch, "E138.left", {"start": v(-132, 34) * mm, "end": v(-132, 46) * mm});
            skLineSegment(sketch, "E138.right", {"start": v(-123.5, 34) * mm, "end": v(-123.5, 46) * mm});
            skLineSegment(sketch, "E139", {"start": v(-136, 34) * mm, "end": v(-132, 34) * mm});
            skLineSegment(sketch, "E140", {"start": v(130.5, 34) * mm, "end": v(126.5, 34) * mm});
            skLineSegment(sketch, "E141.1.0.0", {"start": v(-123.5, 34) * mm, "end": v(-119.5, 34) * mm});
            skLineSegment(sketch, "E141.1.0.1", {"start": v(-111, 34) * mm, "end": v(-111, 46) * mm});
            skLineSegment(sketch, "E141.1.0.2", {"start": v(-119.5, 46) * mm, "end": v(-111, 46) * mm});
            skLineSegment(sketch, "E141.1.0.3", {"start": v(-119.5, 34) * mm, "end": v(-119.5, 46) * mm});
            skLineSegment(sketch, "E141.2.0.0", {"start": v(-111, 34) * mm, "end": v(-107, 34) * mm});
            skLineSegment(sketch, "E141.2.0.1", {"start": v(-98.5, 34) * mm, "end": v(-98.5, 46) * mm});
            skLineSegment(sketch, "E141.2.0.2", {"start": v(-107, 46) * mm, "end": v(-98.5, 46) * mm});
            skLineSegment(sketch, "E141.2.0.3", {"start": v(-107, 34) * mm, "end": v(-107, 46) * mm});
            skLineSegment(sketch, "E141.3.0.0", {"start": v(-98.5, 34) * mm, "end": v(-94.5, 34) * mm});
            skLineSegment(sketch, "E141.3.0.1", {"start": v(-86, 34) * mm, "end": v(-86, 46) * mm});
            skLineSegment(sketch, "E141.3.0.2", {"start": v(-94.5, 46) * mm, "end": v(-86, 46) * mm});
            skLineSegment(sketch, "E141.3.0.3", {"start": v(-94.5, 34) * mm, "end": v(-94.5, 46) * mm});
            skLineSegment(sketch, "E141.4.0.0", {"start": v(-86, 34) * mm, "end": v(-82, 34) * mm});
            skLineSegment(sketch, "E141.4.0.1", {"start": v(-73.5, 34) * mm, "end": v(-73.5, 46) * mm});
            skLineSegment(sketch, "E141.4.0.2", {"start": v(-82, 46) * mm, "end": v(-73.5, 46) * mm});
            skLineSegment(sketch, "E141.4.0.3", {"start": v(-82, 34) * mm, "end": v(-82, 46) * mm});
            skLineSegment(sketch, "E141.5.0.0", {"start": v(-73.5, 34) * mm, "end": v(-69.5, 34) * mm});
            skLineSegment(sketch, "E141.5.0.1", {"start": v(-61, 34) * mm, "end": v(-61, 46) * mm});
            skLineSegment(sketch, "E141.5.0.2", {"start": v(-69.5, 46) * mm, "end": v(-61, 46) * mm});
            skLineSegment(sketch, "E141.5.0.3", {"start": v(-69.5, 34) * mm, "end": v(-69.5, 46) * mm});
            skLineSegment(sketch, "E141.6.0.0", {"start": v(-61, 34) * mm, "end": v(-57, 34) * mm});
            skLineSegment(sketch, "E141.6.0.1", {"start": v(-48.5, 34) * mm, "end": v(-48.5, 46) * mm});
            skLineSegment(sketch, "E141.6.0.2", {"start": v(-57, 46) * mm, "end": v(-48.5, 46) * mm});
            skLineSegment(sketch, "E141.6.0.3", {"start": v(-57, 34) * mm, "end": v(-57, 46) * mm});
            skLineSegment(sketch, "E141.7.0.0", {"start": v(-48.5, 34) * mm, "end": v(-44.5, 34) * mm});
            skLineSegment(sketch, "E141.7.0.1", {"start": v(-36, 34) * mm, "end": v(-36, 46) * mm});
            skLineSegment(sketch, "E141.7.0.2", {"start": v(-44.5, 46) * mm, "end": v(-36, 46) * mm});
            skLineSegment(sketch, "E141.7.0.3", {"start": v(-44.5, 34) * mm, "end": v(-44.5, 46) * mm});
            skLineSegment(sketch, "E141.8.0.0", {"start": v(-36, 34) * mm, "end": v(-32, 34) * mm});
            skLineSegment(sketch, "E141.8.0.1", {"start": v(-23.5, 34) * mm, "end": v(-23.5, 46) * mm});
            skLineSegment(sketch, "E141.8.0.2", {"start": v(-32, 46) * mm, "end": v(-23.5, 46) * mm});
            skLineSegment(sketch, "E141.8.0.3", {"start": v(-32, 34) * mm, "end": v(-32, 46) * mm});
            skLineSegment(sketch, "E141.9.0.0", {"start": v(-23.5, 34) * mm, "end": v(-19.5, 34) * mm});
            skLineSegment(sketch, "E141.9.0.1", {"start": v(-11, 34) * mm, "end": v(-11, 46) * mm});
            skLineSegment(sketch, "E141.9.0.2", {"start": v(-19.5, 46) * mm, "end": v(-11, 46) * mm});
            skLineSegment(sketch, "E141.9.0.3", {"start": v(-19.5, 34) * mm, "end": v(-19.5, 46) * mm});
            skLineSegment(sketch, "E141.10.0.0", {"start": v(-11, 34) * mm, "end": v(-7, 34) * mm});
            skLineSegment(sketch, "E141.10.0.1", {"start": v(1.5, 34) * mm, "end": v(1.5, 46) * mm});
            skLineSegment(sketch, "E141.10.0.2", {"start": v(-7, 46) * mm, "end": v(1.5, 46) * mm});
            skLineSegment(sketch, "E141.10.0.3", {"start": v(-7, 34) * mm, "end": v(-7, 46) * mm});
            skLineSegment(sketch, "E141.11.0.0", {"start": v(1.5, 34) * mm, "end": v(5.5, 34) * mm});
            skLineSegment(sketch, "E141.11.0.1", {"start": v(14, 34) * mm, "end": v(14, 46) * mm});
            skLineSegment(sketch, "E141.11.0.2", {"start": v(5.5, 46) * mm, "end": v(14, 46) * mm});
            skLineSegment(sketch, "E141.11.0.3", {"start": v(5.5, 34) * mm, "end": v(5.5, 46) * mm});
            skLineSegment(sketch, "E141.12.0.0", {"start": v(14, 34) * mm, "end": v(18, 34) * mm});
            skLineSegment(sketch, "E141.12.0.1", {"start": v(26.5, 34) * mm, "end": v(26.5, 46) * mm});
            skLineSegment(sketch, "E141.12.0.2", {"start": v(18, 46) * mm, "end": v(26.5, 46) * mm});
            skLineSegment(sketch, "E141.12.0.3", {"start": v(18, 34) * mm, "end": v(18, 46) * mm});
            skLineSegment(sketch, "E141.13.0.0", {"start": v(26.5, 34) * mm, "end": v(30.5, 34) * mm});
            skLineSegment(sketch, "E141.13.0.1", {"start": v(39, 34) * mm, "end": v(39, 46) * mm});
            skLineSegment(sketch, "E141.13.0.2", {"start": v(30.5, 46) * mm, "end": v(39, 46) * mm});
            skLineSegment(sketch, "E141.13.0.3", {"start": v(30.5, 34) * mm, "end": v(30.5, 46) * mm});
            skLineSegment(sketch, "E141.14.0.0", {"start": v(39, 34) * mm, "end": v(43, 34) * mm});
            skLineSegment(sketch, "E141.14.0.1", {"start": v(51.5, 34) * mm, "end": v(51.5, 46) * mm});
            skLineSegment(sketch, "E141.14.0.2", {"start": v(43, 46) * mm, "end": v(51.5, 46) * mm});
            skLineSegment(sketch, "E141.14.0.3", {"start": v(43, 34) * mm, "end": v(43, 46) * mm});
            skLineSegment(sketch, "E141.15.0.0", {"start": v(51.5, 34) * mm, "end": v(55.5, 34) * mm});
            skLineSegment(sketch, "E141.15.0.1", {"start": v(64, 34) * mm, "end": v(64, 46) * mm});
            skLineSegment(sketch, "E141.15.0.2", {"start": v(55.5, 46) * mm, "end": v(64, 46) * mm});
            skLineSegment(sketch, "E141.15.0.3", {"start": v(55.5, 34) * mm, "end": v(55.5, 46) * mm});
            skLineSegment(sketch, "E141.16.0.0", {"start": v(64, 34) * mm, "end": v(68, 34) * mm});
            skLineSegment(sketch, "E141.16.0.1", {"start": v(76.5, 34) * mm, "end": v(76.5, 46) * mm});
            skLineSegment(sketch, "E141.16.0.2", {"start": v(68, 46) * mm, "end": v(76.5, 46) * mm});
            skLineSegment(sketch, "E141.16.0.3", {"start": v(68, 34) * mm, "end": v(68, 46) * mm});
            skLineSegment(sketch, "E141.17.0.0", {"start": v(76.5, 34) * mm, "end": v(80.5, 34) * mm});
            skLineSegment(sketch, "E141.17.0.1", {"start": v(89, 34) * mm, "end": v(89, 46) * mm});
            skLineSegment(sketch, "E141.17.0.2", {"start": v(80.5, 46) * mm, "end": v(89, 46) * mm});
            skLineSegment(sketch, "E141.17.0.3", {"start": v(80.5, 34) * mm, "end": v(80.5, 46) * mm});
            skLineSegment(sketch, "E141.18.0.0", {"start": v(89, 34) * mm, "end": v(93, 34) * mm});
            skLineSegment(sketch, "E141.18.0.1", {"start": v(101.5, 34) * mm, "end": v(101.5, 46) * mm});
            skLineSegment(sketch, "E141.18.0.2", {"start": v(93, 46) * mm, "end": v(101.5, 46) * mm});
            skLineSegment(sketch, "E141.18.0.3", {"start": v(93, 34) * mm, "end": v(93, 46) * mm});
            skLineSegment(sketch, "E141.19.0.0", {"start": v(101.5, 34) * mm, "end": v(105.5, 34) * mm});
            skLineSegment(sketch, "E141.19.0.1", {"start": v(114, 34) * mm, "end": v(114, 46) * mm});
            skLineSegment(sketch, "E141.19.0.2", {"start": v(105.5, 46) * mm, "end": v(114, 46) * mm});
            skLineSegment(sketch, "E141.19.0.3", {"start": v(105.5, 34) * mm, "end": v(105.5, 46) * mm});
            skLineSegment(sketch, "E141.20.0.0", {"start": v(114, 34) * mm, "end": v(118, 34) * mm});
            skLineSegment(sketch, "E141.20.0.1", {"start": v(126.5, 34) * mm, "end": v(126.5, 46) * mm});
            skLineSegment(sketch, "E141.20.0.2", {"start": v(118, 46) * mm, "end": v(126.5, 46) * mm});
            skLineSegment(sketch, "E141.20.0.3", {"start": v(118, 34) * mm, "end": v(118, 46) * mm});
            skLineSegment(sketch, "E142.MirrorCS", {"start": v(151, 34) * mm, "end": v(155, 34) * mm});
            skLineSegment(sketch, "E143.MirrorCS", {"start": v(151, 16) * mm, "end": v(155, 16) * mm});
            skLineSegment(sketch, "E144.MirrorCS", {"start": v(151, 16) * mm, "end": v(151, 4) * mm});
            skLineSegment(sketch, "E145", {"start": v(151, 46) * mm, "end": v(130.5, 46) * mm});
            skLineSegment(sketch, "E146", {"start": v(-151, 4) * mm, "end": v(151, 4) * mm});
            skLineSegment(sketch, "E147.bottom", {"start": v(-109, 4) * mm, "end": v(-89, 4) * mm});
            skLineSegment(sketch, "E147.top", {"start": v(-109, 0) * mm, "end": v(-89, 0) * mm});
            skLineSegment(sketch, "E147.left", {"start": v(-109, 4) * mm, "end": v(-109, 0) * mm});
            skLineSegment(sketch, "E147.right", {"start": v(-89, 4) * mm, "end": v(-89, 0) * mm});
            skLineSegment(sketch, "E148.1.0.0", {"start": v(-43, 0) * mm, "end": v(-23, 0) * mm});
            skLineSegment(sketch, "E148.1.0.1", {"start": v(-43, 4) * mm, "end": v(-23, 4) * mm});
            skLineSegment(sketch, "E148.1.0.2", {"start": v(-23, 4) * mm, "end": v(-23, 0) * mm});
            skLineSegment(sketch, "E148.1.0.3", {"start": v(-43, 4) * mm, "end": v(-43, 0) * mm});
            skLineSegment(sketch, "E148.2.0.0", {"start": v(23, 0) * mm, "end": v(43, 0) * mm});
            skLineSegment(sketch, "E148.2.0.1", {"start": v(23, 4) * mm, "end": v(43, 4) * mm});
            skLineSegment(sketch, "E148.2.0.2", {"start": v(43, 4) * mm, "end": v(43, 0) * mm});
            skLineSegment(sketch, "E148.2.0.3", {"start": v(23, 4) * mm, "end": v(23, 0) * mm});
            skLineSegment(sketch, "E148.3.0.0", {"start": v(89, 0) * mm, "end": v(109, 0) * mm});
            skLineSegment(sketch, "E148.3.0.1", {"start": v(89, 4) * mm, "end": v(109, 4) * mm});
            skLineSegment(sketch, "E148.3.0.2", {"start": v(109, 4) * mm, "end": v(109, 0) * mm});
            skLineSegment(sketch, "E148.3.0.3", {"start": v(89, 4) * mm, "end": v(89, 0) * mm});
            skLineSegment(sketch, "E148.direction1", {"start": v(-109, 0) * mm, "end": v(-43, 0) * mm, "construction": true});
            skLineSegment(sketch, "E149.bottom", {"start": v(14, 26) * mm, "end": v(18, 26) * mm});
            skLineSegment(sketch, "E149.top", {"start": v(14, 14) * mm, "end": v(18, 14) * mm});
            skLineSegment(sketch, "E149.left", {"start": v(14, 26) * mm, "end": v(14, 14) * mm});
            skLineSegment(sketch, "E149.right", {"start": v(18, 26) * mm, "end": v(18, 14) * mm});
            skLineSegment(sketch, "E150.bottom", {"start": v(43, 26) * mm, "end": v(47, 26) * mm});
            skLineSegment(sketch, "E150.top", {"start": v(43, 14) * mm, "end": v(47, 14) * mm});
            skLineSegment(sketch, "E150.left", {"start": v(43, 26) * mm, "end": v(43, 14) * mm});
            skLineSegment(sketch, "E150.right", {"start": v(47, 26) * mm, "end": v(47, 14) * mm});
            skLineSegment(sketch, "E151", {"start": v(-151, 34) * mm, "end": v(-151, 46) * mm});
            skLineSegment(sketch, "E152", {"start": v(151, 46) * mm, "end": v(151, 34) * mm});
            skLineSegment(sketch, "E153", {"start": v(-151, 46) * mm, "end": v(-136, 46) * mm});
            skSolve(sketch);
        }
        {
            var Q0;
            Q0 = qSketchRegion(id + "F5", true);
            extrude(context, id + "F6", {"entities" : qUnion([Q0]), "oppositeDirection" : true, "depth" : 4 * mm});
        }
        {
            var Q0;
            Q0=qCreatedBy(makeId("Front.planeOp"),FACE);
            var sketch = newSketch(context, id + "F7", { "sketchPlane" : qUnion([Q0])});
            skLineSegment(sketch, "E154", {"start": v(-57, 46) * mm, "end": v(-63, 46) * mm, "construction": true});
            skLineSegment(sketch, "E155", {"start": v(-63, 46) * mm, "end": v(-63, 26) * mm});
            skLineSegment(sketch, "E156", {"start": v(-63, 26) * mm, "end": v(-67, 26) * mm});
            skLineSegment(sketch, "E157", {"start": v(-67, 26) * mm, "end": v(-67, 14) * mm});
            skLineSegment(sketch, "E158", {"start": v(-67, 14) * mm, "end": v(-63, 14) * mm});
            skLineSegment(sketch, "E159", {"start": v(-63, 14) * mm, "end": v(-63, 4) * mm});
            skLineSegment(sketch, "E160", {"start": v(-63, 4) * mm, "end": v(-29, 4) * mm});
            skLineSegment(sketch, "E161", {"start": v(-29, 4) * mm, "end": v(-29, 0) * mm});
            skLineSegment(sketch, "E162", {"start": v(-29, 0) * mm, "end": v(-9, 0) * mm});
            skLineSegment(sketch, "E163", {"start": v(-9, 0) * mm, "end": v(-9, 4) * mm});
            skLineSegment(sketch, "E164", {"start": v(-9, 4) * mm, "end": v(25, 4) * mm});
            skLineSegment(sketch, "E165", {"start": v(25, 4) * mm, "end": v(25, 14) * mm});
            skLineSegment(sketch, "E166", {"start": v(25, 14) * mm, "end": v(29, 14) * mm});
            skLineSegment(sketch, "E167", {"start": v(29, 14) * mm, "end": v(29, 26) * mm});
            skLineSegment(sketch, "E168", {"start": v(29, 26) * mm, "end": v(25, 26) * mm});
            skLineSegment(sketch, "E169", {"start": v(25, 26) * mm, "end": v(25, 46) * mm});
            skLineSegment(sketch, "E170", {"start": v(25, 46) * mm, "end": v(19, 46) * mm, "construction": true});
            skLineSegment(sketch, "E171", {"start": v(-26, 46) * mm, "end": v(-19, 46) * mm, "construction": true});
            skLineSegment(sketch, "E172", {"start": v(-19, 46) * mm, "end": v(-12, 46) * mm, "construction": true});
            skLineSegment(sketch, "E173", {"start": v(-57, 46) * mm, "end": v(-26, 46) * mm, "construction": true});
            skLineSegment(sketch, "E174", {"start": v(-12, 46) * mm, "end": v(19, 46) * mm, "construction": true});
            skLineSegment(sketch, "E175", {"start": v(-19, 53.52) * mm, "end": v(-19, -5.95) * mm, "construction": true});
            skLineSegment(sketch, "E176.bottom", {"start": v(-21, 26) * mm, "end": v(-17, 26) * mm});
            skLineSegment(sketch, "E176.top", {"start": v(-21, 14) * mm, "end": v(-17, 14) * mm});
            skLineSegment(sketch, "E176.left", {"start": v(-21, 26) * mm, "end": v(-21, 14) * mm});
            skLineSegment(sketch, "E176.right", {"start": v(-17, 26) * mm, "end": v(-17, 14) * mm});
            skLineSegment(sketch, "E177", {"start": v(-63, 46) * mm, "end": v(-60.59, 46) * mm});
            skLineSegment(sketch, "E178", {"start": v(-22.41, 46) * mm, "end": v(-19, 46) * mm});
            skArc(sketch, "E179", {"start": v(-56.67, 42.82) * mm, "mid": v(-41.5, 30.5) * mm, "end": v(-26.33, 42.82) * mm});
            skPoint(sketch, "E180.visualSharp", {"position": v(-57, 46) * mm});
            skArc(sketch, "E180.filletArc", {"start": v(-56.67, 42.82) * mm, "mid": v(-58.06, 45.1) * mm, "end": v(-60.59, 46) * mm});
            skPoint(sketch, "E181.visualSharp", {"position": v(-26, 46) * mm});
            skArc(sketch, "E181.filletArc", {"start": v(-22.41, 46) * mm, "mid": v(-24.94, 45.1) * mm, "end": v(-26.33, 42.82) * mm});
            skLineSegment(sketch, "E182", {"start": v(-19, 46) * mm, "end": v(-15.44, 46) * mm});
            skLineSegment(sketch, "E183", {"start": v(22.73, 46) * mm, "end": v(25, 46) * mm});
            skArc(sketch, "E184", {"start": v(-11.52, 42.82) * mm, "mid": v(3.65, 30.5) * mm, "end": v(18.82, 42.82) * mm});
            skLineSegment(sketch, "E185", {"start": v(-11.85, 46) * mm, "end": v(19.15, 46) * mm, "construction": true});
            skPoint(sketch, "E186.visualSharp", {"position": v(-11.85, 46) * mm});
            skArc(sketch, "E186.filletArc", {"start": v(-11.52, 42.82) * mm, "mid": v(-12.92, 45.1) * mm, "end": v(-15.44, 46) * mm});
            skPoint(sketch, "E187.visualSharp", {"position": v(19.15, 46) * mm});
            skArc(sketch, "E187.filletArc", {"start": v(22.73, 46) * mm, "mid": v(20.21, 45.1) * mm, "end": v(18.82, 42.82) * mm});
            skSolve(sketch);
        }
        {
            var Q0;
            Q0 = qSketchRegion(id + "F7", true);
            extrude(context, id + "F8", {"entities" : qUnion([Q0]), "depth" : 4 * mm});
        }
        {
            var Q0;
            Q0=qCreatedBy(makeId("Right.planeOp"),FACE);
            var sketch = newSketch(context, id + "F9", { "sketchPlane" : qUnion([Q0])});
            skLineSegment(sketch, "E188.bottom", {"start": v(18, 46) * mm, "end": v(43, 46) * mm});
            skLineSegment(sketch, "E188.top", {"start": v(18, 4) * mm, "end": v(43, 4) * mm});
            skLineSegment(sketch, "E188.left", {"start": v(18, 46) * mm, "end": v(18, 4) * mm});
            skLineSegment(sketch, "E188.right", {"start": v(43, 46) * mm, "end": v(43, 4) * mm});
            skLineSegment(sketch, "E189.bottom", {"start": v(18, 26) * mm, "end": v(14, 26) * mm});
            skLineSegment(sketch, "E189.top", {"start": v(18, 14) * mm, "end": v(14, 14) * mm});
            skLineSegment(sketch, "E189.left", {"start": v(18, 26) * mm, "end": v(18, 14) * mm});
            skLineSegment(sketch, "E189.right", {"start": v(14, 26) * mm, "end": v(14, 14) * mm});
            skPoint(sketch, "E190.firstSnap0", {"position": v(16, 14) * mm});
            skLineSegment(sketch, "E190.bottom", {"start": v(43, 14) * mm, "end": v(47, 14) * mm});
            skLineSegment(sketch, "E190.top", {"start": v(43, 26) * mm, "end": v(47, 26) * mm});
            skLineSegment(sketch, "E190.left", {"start": v(43, 14) * mm, "end": v(43, 26) * mm});
            skLineSegment(sketch, "E190.right", {"start": v(47, 14) * mm, "end": v(47, 26) * mm});
            skSolve(sketch);
        }
        {
            var Q0;
            Q0 = qSketchRegion(id + "F9", true);
            extrude(context, id + "F10", {"entities" : qUnion([Q0]), "depth" : 4 * mm});
        }
        {
            var Q0;
            Q0=qCreatedBy(makeId("Front.planeOp"),FACE);
            var sketch = newSketch(context, id + "F11", { "sketchPlane" : qUnion([Q0])});
            skLineSegment(sketch, "E191.top", {"start": v(-106, 4) * mm, "end": v(106, 4) * mm});
            skLineSegment(sketch, "E191.left", {"start": v(-106, 46) * mm, "end": v(-106, 4) * mm});
            skLineSegment(sketch, "E191.right", {"start": v(106, 46) * mm, "end": v(106, 4) * mm});
            skLineSegment(sketch, "E192", {"start": v(106, 46) * mm, "end": v(90.5, 46) * mm, "construction": true});
            skLineSegment(sketch, "E193", {"start": v(-101.5, 46) * mm, "end": v(-106, 46) * mm});
            skArc(sketch, "E194", {"start": v(44.5, 46) * mm, "mid": v(67.5, 23) * mm, "end": v(90.5, 46) * mm, "construction": true});
            skLineSegment(sketch, "E195", {"start": v(29, 65.47) * mm, "end": v(29, 0) * mm, "construction": true});
            skLineSegment(sketch, "E196", {"start": v(-67, 0) * mm, "end": v(-67, 80.2) * mm, "construction": true});
            skLineSegment(sketch, "E197", {"start": v(44.5, 46) * mm, "end": v(29, 46) * mm, "construction": true});
            skLineSegment(sketch, "E198", {"start": v(29, 46) * mm, "end": v(-67, 46) * mm});
            skLineSegment(sketch, "E199", {"start": v(-67, 46) * mm, "end": v(-71.5, 46) * mm});
            skLineSegment(sketch, "E200", {"start": v(110, 23) * mm, "end": v(-110, 23) * mm, "construction": true});
            skLineSegment(sketch, "E201", {"start": v(-75.5, 42) * mm, "end": v(-75.5, 34) * mm});
            skLineSegment(sketch, "E202", {"start": v(-97.5, 42) * mm, "end": v(-97.5, 34) * mm});
            skArc(sketch, "E203", {"start": v(-97.5, 34) * mm, "mid": v(-86.5, 23) * mm, "end": v(-75.5, 34) * mm});
            skLineSegment(sketch, "E204", {"start": v(-75.5, 34) * mm, "end": v(-97.5, 34) * mm, "construction": true});
            skLineSegment(sketch, "E205", {"start": v(90.5, 46) * mm, "end": v(90.5, 23) * mm, "construction": true});
            skLineSegment(sketch, "E206", {"start": v(90.5, 23) * mm, "end": v(90.5, 0) * mm, "construction": true});
            skPoint(sketch, "E207.oppositeSnap0", {"position": v(90.5, 11.5) * mm});
            skLineSegment(sketch, "E208", {"start": v(16, 40) * mm, "end": v(-16, 40) * mm});
            skLineSegment(sketch, "E209", {"start": v(0, 40) * mm, "end": v(0, 0) * mm, "construction": true});
            skArc(sketch, "E210", {"start": v(-16, 40) * mm, "mid": v(0, 30.25) * mm, "end": v(16, 40) * mm});
            skLineSegment(sketch, "E211.bottom", {"start": v(-88, 4) * mm, "end": v(-77, 4) * mm});
            skLineSegment(sketch, "E211.top", {"start": v(-88, 0) * mm, "end": v(-77, 0) * mm});
            skLineSegment(sketch, "E211.left", {"start": v(-88, 4) * mm, "end": v(-88, 0) * mm});
            skLineSegment(sketch, "E211.right", {"start": v(-77, 4) * mm, "end": v(-77, 0) * mm});
            skLineSegment(sketch, "E212.bottom", {"start": v(-55, 4) * mm, "end": v(-44, 4) * mm});
            skLineSegment(sketch, "E212.top", {"start": v(-55, 0) * mm, "end": v(-44, 0) * mm});
            skLineSegment(sketch, "E212.left", {"start": v(-55, 4) * mm, "end": v(-55, 0) * mm});
            skLineSegment(sketch, "E212.right", {"start": v(-44, 4) * mm, "end": v(-44, 0) * mm});
            skLineSegment(sketch, "E213.bottom", {"start": v(-22, 4) * mm, "end": v(-11, 4) * mm});
            skLineSegment(sketch, "E213.top", {"start": v(-22, 0) * mm, "end": v(-11, 0) * mm});
            skLineSegment(sketch, "E213.left", {"start": v(-22, 4) * mm, "end": v(-22, 0) * mm});
            skLineSegment(sketch, "E213.right", {"start": v(-11, 4) * mm, "end": v(-11, 0) * mm});
            skLineSegment(sketch, "E214.bottom", {"start": v(11, 4) * mm, "end": v(22, 4) * mm});
            skLineSegment(sketch, "E214.top", {"start": v(11, 0) * mm, "end": v(22, 0) * mm});
            skLineSegment(sketch, "E214.left", {"start": v(11, 4) * mm, "end": v(11, 0) * mm});
            skLineSegment(sketch, "E214.right", {"start": v(22, 4) * mm, "end": v(22, 0) * mm});
            skLineSegment(sketch, "E215.bottom", {"start": v(44, 4) * mm, "end": v(55, 4) * mm});
            skLineSegment(sketch, "E215.top", {"start": v(44, 0) * mm, "end": v(55, 0) * mm});
            skLineSegment(sketch, "E215.left", {"start": v(44, 4) * mm, "end": v(44, 0) * mm});
            skLineSegment(sketch, "E215.right", {"start": v(55, 4) * mm, "end": v(55, 0) * mm});
            skLineSegment(sketch, "E216.bottom", {"start": v(77, 4) * mm, "end": v(88, 4) * mm});
            skLineSegment(sketch, "E216.top", {"start": v(77, 0) * mm, "end": v(88, 0) * mm});
            skLineSegment(sketch, "E216.left", {"start": v(77, 4) * mm, "end": v(77, 0) * mm});
            skLineSegment(sketch, "E216.right", {"start": v(88, 4) * mm, "end": v(88, 0) * mm});
            skLineSegment(sketch, "E217", {"start": v(106, 34) * mm, "end": v(110, 34) * mm});
            skLineSegment(sketch, "E218", {"start": v(110, 34) * mm, "end": v(110, 16) * mm});
            skLineSegment(sketch, "E219", {"start": v(110, 16) * mm, "end": v(106, 16) * mm});
            skLineSegment(sketch, "E220", {"start": v(-106, 34) * mm, "end": v(-110, 34) * mm});
            skLineSegment(sketch, "E221", {"start": v(-110, 34) * mm, "end": v(-110, 16) * mm});
            skLineSegment(sketch, "E222", {"start": v(-110, 16) * mm, "end": v(-106, 16) * mm});
            skLineSegment(sketch, "E223.bottom", {"start": v(-67, 34) * mm, "end": v(-63, 34) * mm});
            skLineSegment(sketch, "E223.top", {"start": v(-67, 16) * mm, "end": v(-63, 16) * mm});
            skLineSegment(sketch, "E223.left", {"start": v(-67, 34) * mm, "end": v(-67, 16) * mm});
            skLineSegment(sketch, "E223.right", {"start": v(-63, 34) * mm, "end": v(-63, 16) * mm});
            skLineSegment(sketch, "E224.bottom", {"start": v(29, 34) * mm, "end": v(25, 34) * mm});
            skLineSegment(sketch, "E224.top", {"start": v(29, 16) * mm, "end": v(25, 16) * mm});
            skLineSegment(sketch, "E224.left", {"start": v(29, 34) * mm, "end": v(29, 16) * mm});
            skLineSegment(sketch, "E224.right", {"start": v(25, 34) * mm, "end": v(25, 16) * mm});
            skLineSegment(sketch, "E225", {"start": v(106, 46) * mm, "end": v(94.2, 46) * mm});
            skLineSegment(sketch, "E226", {"start": v(40.8, 46) * mm, "end": v(29, 46) * mm});
            skLineSegment(sketch, "E227", {"start": v(90.5, 46) * mm, "end": v(44.5, 46) * mm, "construction": true});
            skArc(sketch, "E228", {"start": v(44.75, 42.6) * mm, "mid": v(67.5, 23) * mm, "end": v(90.25, 42.6) * mm});
            skPoint(sketch, "E229.visualSharp", {"position": v(44.5, 46) * mm});
            skArc(sketch, "E229.filletArc", {"start": v(44.75, 42.6) * mm, "mid": v(43.4, 45.03) * mm, "end": v(40.8, 46) * mm});
            skPoint(sketch, "E230.visualSharp", {"position": v(90.5, 46) * mm});
            skArc(sketch, "E230.filletArc", {"start": v(94.2, 46) * mm, "mid": v(91.6, 45.03) * mm, "end": v(90.25, 42.6) * mm});
            skLineSegment(sketch, "E231", {"start": v(67.5, 46) * mm, "end": v(60.34, 24.14) * mm, "construction": true});
            skLineSegment(sketch, "E232", {"start": v(67.5, 46) * mm, "end": v(50.22, 30.82) * mm, "construction": true});
            skPoint(sketch, "E233.visualSharp", {"position": v(-75.5, 46) * mm});
            skArc(sketch, "E233.filletArc", {"start": v(-71.5, 46) * mm, "mid": v(-74.33, 44.83) * mm, "end": v(-75.5, 42) * mm});
            skPoint(sketch, "E234.visualSharp", {"position": v(-97.5, 46) * mm});
            skArc(sketch, "E234.filletArc", {"start": v(-97.5, 42) * mm, "mid": v(-98.67, 44.83) * mm, "end": v(-101.5, 46) * mm});
            skSolve(sketch);
        }
        {
            var Q0;
            Q0 = qSketchRegion(id + "F11", true);
            extrude(context, id + "F12", {"entities" : qUnion([Q0]), "depth" : 4 * mm});
        }
        {
            var Q0;
            Q0=qCreatedBy(makeId("Front.planeOp"),FACE);
            var sketch = newSketch(context, id + "F13", { "sketchPlane" : qUnion([Q0])});
            skLineSegment(sketch, "E235.top", {"start": v(-106, 4) * mm, "end": v(-88, 4) * mm});
            skLineSegment(sketch, "E236.bottom", {"start": v(-106, 34) * mm, "end": v(-110, 34) * mm});
            skLineSegment(sketch, "E236.top", {"start": v(-106, 16) * mm, "end": v(-110, 16) * mm});
            skLineSegment(sketch, "E237.bottom", {"start": v(106, 34) * mm, "end": v(110, 34) * mm});
            skLineSegment(sketch, "E237.top", {"start": v(106, 16) * mm, "end": v(110, 16) * mm});
            skLineSegment(sketch, "E238", {"start": v(29, 65.47) * mm, "end": v(29, 4) * mm, "construction": true});
            skLineSegment(sketch, "E239", {"start": v(-67, 0) * mm, "end": v(-67, 80.2) * mm, "construction": true});
            skLineSegment(sketch, "E240.bottom", {"start": v(29, 34) * mm, "end": v(25, 34) * mm});
            skLineSegment(sketch, "E240.top", {"start": v(29, 16) * mm, "end": v(25, 16) * mm});
            skLineSegment(sketch, "E240.left", {"start": v(29, 34) * mm, "end": v(29, 16) * mm});
            skLineSegment(sketch, "E240.right", {"start": v(25, 34) * mm, "end": v(25, 16) * mm});
            skLineSegment(sketch, "E241.bottom", {"start": v(-67, 34) * mm, "end": v(-63, 34) * mm});
            skLineSegment(sketch, "E241.top", {"start": v(-67, 16) * mm, "end": v(-63, 16) * mm});
            skLineSegment(sketch, "E241.left", {"start": v(-67, 34) * mm, "end": v(-67, 16) * mm});
            skLineSegment(sketch, "E241.right", {"start": v(-63, 34) * mm, "end": v(-63, 16) * mm});
            skLineSegment(sketch, "E242", {"start": v(16, 40) * mm, "end": v(-16, 40) * mm});
            skLineSegment(sketch, "E243", {"start": v(0, 40) * mm, "end": v(0, 0) * mm, "construction": true});
            skArc(sketch, "E244", {"start": v(-16, 40) * mm, "mid": v(0, 30.25) * mm, "end": v(16, 40) * mm});
            skLineSegment(sketch, "E245", {"start": v(-9, 66.76) * mm, "end": v(-9, -62.6) * mm, "construction": true});
            skLineSegment(sketch, "E246", {"start": v(-29, 66.35) * mm, "end": v(-29, -69.55) * mm, "construction": true});
            skLineSegment(sketch, "E247.bottom", {"start": v(88, 0) * mm, "end": v(77, 0) * mm});
            skLineSegment(sketch, "E247.left", {"start": v(88, 0) * mm, "end": v(88, 4) * mm});
            skLineSegment(sketch, "E247.right", {"start": v(77, 0) * mm, "end": v(77, 4) * mm});
            skLineSegment(sketch, "E248.bottom", {"start": v(55, 0) * mm, "end": v(44, 0) * mm});
            skLineSegment(sketch, "E248.left", {"start": v(55, 0) * mm, "end": v(55, 4) * mm});
            skLineSegment(sketch, "E248.right", {"start": v(44, 0) * mm, "end": v(44, 4) * mm});
            skLineSegment(sketch, "E249.bottom", {"start": v(22, 0) * mm, "end": v(11, 0) * mm});
            skLineSegment(sketch, "E249.left", {"start": v(22, 0) * mm, "end": v(22, 4) * mm});
            skLineSegment(sketch, "E249.right", {"start": v(11, 0) * mm, "end": v(11, 4) * mm});
            skLineSegment(sketch, "E250.bottom", {"start": v(-44, 0) * mm, "end": v(-55, 0) * mm});
            skLineSegment(sketch, "E250.left", {"start": v(-44, 0) * mm, "end": v(-44, 4) * mm});
            skLineSegment(sketch, "E250.right", {"start": v(-55, 0) * mm, "end": v(-55, 4) * mm});
            skLineSegment(sketch, "E251.bottom", {"start": v(-77, 0) * mm, "end": v(-88, 0) * mm});
            skLineSegment(sketch, "E251.left", {"start": v(-77, 0) * mm, "end": v(-77, 4) * mm});
            skLineSegment(sketch, "E251.right", {"start": v(-88, 0) * mm, "end": v(-88, 4) * mm});
            skLineSegment(sketch, "E252.trimOffspring", {"start": v(-9, 4) * mm, "end": v(11, 4) * mm});
            skLineSegment(sketch, "E253.trimOffspring", {"start": v(88, 4) * mm, "end": v(106, 4) * mm});
            skLineSegment(sketch, "E254.trimOffspring", {"start": v(55, 4) * mm, "end": v(77, 4) * mm});
            skLineSegment(sketch, "E255.trimOffspring", {"start": v(22, 4) * mm, "end": v(44, 4) * mm});
            skLineSegment(sketch, "E256.trimOffspring", {"start": v(-44, 4) * mm, "end": v(-29, 4) * mm});
            skLineSegment(sketch, "E257.trimOffspring", {"start": v(-77, 4) * mm, "end": v(-55, 4) * mm});
            skLineSegment(sketch, "E258.right", {"start": v(110, 46) * mm, "end": v(110, 34) * mm});
            skLineSegment(sketch, "E259.bottom", {"start": v(110, 16) * mm, "end": v(106, 16) * mm});
            skLineSegment(sketch, "E259.top", {"start": v(110, 4) * mm, "end": v(106, 4) * mm});
            skLineSegment(sketch, "E259.left", {"start": v(110, 16) * mm, "end": v(110, 4) * mm});
            skLineSegment(sketch, "E260.bottom", {"start": v(-106, 4) * mm, "end": v(-110, 4) * mm});
            skLineSegment(sketch, "E260.right", {"start": v(-110, 4) * mm, "end": v(-110, 16) * mm});
            skLineSegment(sketch, "E261.bottom", {"start": v(-110, 34) * mm, "end": v(-106, 34) * mm});
            skLineSegment(sketch, "E261.left", {"start": v(-110, 34) * mm, "end": v(-110, 46) * mm});
            skLineSegment(sketch, "E262", {"start": v(106, 34) * mm, "end": v(106, 16) * mm});
            skLineSegment(sketch, "E263", {"start": v(-106, 34) * mm, "end": v(-106, 16) * mm});
            skLineSegment(sketch, "E264", {"start": v(94.2, 46) * mm, "end": v(110, 46) * mm});
            skLineSegment(sketch, "E265", {"start": v(-71.5, 46) * mm, "end": v(40.8, 46) * mm});
            skLineSegment(sketch, "E266", {"start": v(-110, 46) * mm, "end": v(-101.5, 46) * mm});
            skLineSegment(sketch, "E267", {"start": v(-29, 4) * mm, "end": v(-29, 12) * mm});
            skLineSegment(sketch, "E268", {"start": v(-9, 4) * mm, "end": v(-9, 12) * mm});
            skArc(sketch, "E269", {"start": v(-9, 12) * mm, "mid": v(-19, 22) * mm, "end": v(-29, 12) * mm});
            skLineSegment(sketch, "E270", {"start": v(-29, 12) * mm, "end": v(-9, 12) * mm, "construction": true});
            skArc(sketch, "E271", {"start": v(44.75, 42.6) * mm, "mid": v(67.5, 23) * mm, "end": v(90.25, 42.6) * mm});
            skLineSegment(sketch, "E272", {"start": v(-75.5, 42) * mm, "end": v(-75.5, 34) * mm});
            skLineSegment(sketch, "E273", {"start": v(-97.5, 42) * mm, "end": v(-97.5, 34) * mm});
            skArc(sketch, "E274", {"start": v(-97.5, 34) * mm, "mid": v(-86.5, 23) * mm, "end": v(-75.5, 34) * mm});
            skPoint(sketch, "E275.visualSharp", {"position": v(-75.5, 46) * mm});
            skArc(sketch, "E275.filletArc", {"start": v(-71.5, 46) * mm, "mid": v(-74.33, 44.83) * mm, "end": v(-75.5, 42) * mm});
            skPoint(sketch, "E276.visualSharp", {"position": v(-97.5, 46) * mm});
            skArc(sketch, "E276.filletArc", {"start": v(-97.5, 42) * mm, "mid": v(-98.67, 44.83) * mm, "end": v(-101.5, 46) * mm});
            skPoint(sketch, "E277.visualSharp", {"position": v(90.5, 46) * mm});
            skArc(sketch, "E277.filletArc", {"start": v(94.2, 46) * mm, "mid": v(91.6, 45.03) * mm, "end": v(90.25, 42.6) * mm});
            skPoint(sketch, "E278.visualSharp", {"position": v(44.5, 46) * mm});
            skArc(sketch, "E278.filletArc", {"start": v(44.75, 42.6) * mm, "mid": v(43.4, 45.03) * mm, "end": v(40.8, 46) * mm});
            skSolve(sketch);
        }
        {
            var Q0;
            Q0 = qSketchRegion(id + "F13", true);
            extrude(context, id + "F14", {"entities" : qUnion([Q0]), "oppositeDirection" : true, "depth" : 4 * mm});
        }
        {
            var Q0;
            Q0=qCreatedBy(makeId("Right.planeOp"),FACE);
            var sketch = newSketch(context, id + "F15", { "sketchPlane" : qUnion([Q0])});
            skLineSegment(sketch, "E279.bottom", {"start": v(47, 12) * mm, "end": v(151, 12) * mm});
            skLineSegment(sketch, "E279.top", {"start": v(47, 4) * mm, "end": v(151, 4) * mm});
            skLineSegment(sketch, "E279.left", {"start": v(47, 12) * mm, "end": v(47, 4) * mm});
            skLineSegment(sketch, "E279.right", {"start": v(151, 12) * mm, "end": v(151, 4) * mm});
            skLineSegment(sketch, "E280.bottom", {"start": v(89, 4) * mm, "end": v(109, 4) * mm});
            skLineSegment(sketch, "E280.top", {"start": v(89, 0) * mm, "end": v(109, 0) * mm});
            skLineSegment(sketch, "E280.left", {"start": v(89, 4) * mm, "end": v(89, 0) * mm});
            skLineSegment(sketch, "E280.right", {"start": v(109, 4) * mm, "end": v(109, 0) * mm});
            skSolve(sketch);
        }
        {
            var Q0;
            Q0 = qSketchRegion(id + "F15", true);
            extrude(context, id + "F16", {"entities" : qUnion([Q0]), "depth" : 4 * mm});
        }
        {
            var Q0;
            Q0=qCreatedBy(makeId("Top.planeOp"),FACE);
            var sketch = newSketch(context, id + "F17", { "sketchPlane" : qUnion([Q0])});
            skLineSegment(sketch, "E281.bottom", {"start": v(-59, 146.5) * mm, "end": v(20.5, 146.5) * mm});
            skLineSegment(sketch, "E281.top", {"start": v(-59, 51) * mm, "end": v(20.5, 51) * mm});
            skLineSegment(sketch, "E281.left", {"start": v(-59, 146.5) * mm, "end": v(-59, 51) * mm});
            skLineSegment(sketch, "E281.right", {"start": v(20.5, 146.5) * mm, "end": v(20.5, 51) * mm});
            skLineSegment(sketch, "E282.bottom", {"start": v(20.5, 150.5) * mm, "end": v(24.5, 150.5) * mm});
            skLineSegment(sketch, "E282.top", {"start": v(20.5, 137.5) * mm, "end": v(24.5, 137.5) * mm});
            skLineSegment(sketch, "E282.left", {"start": v(20.5, 150.5) * mm, "end": v(20.5, 137.5) * mm});
            skLineSegment(sketch, "E282.right", {"start": v(24.5, 150.5) * mm, "end": v(24.5, 137.5) * mm});
            skLineSegment(sketch, "E283.bottom", {"start": v(12.4, 146.5) * mm, "end": v(24.5, 146.5) * mm});
            skLineSegment(sketch, "E283.top", {"start": v(12.4, 150.5) * mm, "end": v(24.5, 150.5) * mm});
            skLineSegment(sketch, "E283.left", {"start": v(12.4, 146.5) * mm, "end": v(12.4, 150.5) * mm});
            skLineSegment(sketch, "E283.right", {"start": v(24.5, 146.5) * mm, "end": v(24.5, 150.5) * mm});
            skLineSegment(sketch, "E284.1.0.0", {"start": v(-12.73, 150.5) * mm, "end": v(-0.63, 150.5) * mm});
            skLineSegment(sketch, "E284.1.0.1", {"start": v(-12.73, 146.5) * mm, "end": v(-0.63, 146.5) * mm});
            skLineSegment(sketch, "E284.1.0.2", {"start": v(-12.73, 146.5) * mm, "end": v(-12.73, 150.5) * mm});
            skLineSegment(sketch, "E284.1.0.3", {"start": v(-0.63, 146.5) * mm, "end": v(-0.63, 150.5) * mm});
            skLineSegment(sketch, "E284.1.0.4", {"start": v(-4.63, 150.5) * mm, "end": v(-0.63, 150.5) * mm});
            skLineSegment(sketch, "E284.2.0.0", {"start": v(-37.87, 150.5) * mm, "end": v(-25.77, 150.5) * mm});
            skLineSegment(sketch, "E284.2.0.1", {"start": v(-37.87, 146.5) * mm, "end": v(-25.77, 146.5) * mm});
            skLineSegment(sketch, "E284.2.0.2", {"start": v(-37.87, 146.5) * mm, "end": v(-37.87, 150.5) * mm});
            skLineSegment(sketch, "E284.2.0.3", {"start": v(-25.77, 146.5) * mm, "end": v(-25.77, 150.5) * mm});
            skLineSegment(sketch, "E284.2.0.4", {"start": v(-29.77, 150.5) * mm, "end": v(-25.77, 150.5) * mm});
            skLineSegment(sketch, "E284.3.0.0", {"start": v(-50.9, 150.5) * mm, "end": v(-63, 150.5) * mm});
            skLineSegment(sketch, "E284.3.0.1", {"start": v(-63, 146.5) * mm, "end": v(-50.9, 146.5) * mm});
            skLineSegment(sketch, "E284.3.0.2", {"start": v(-63, 146.5) * mm, "end": v(-63, 150.5) * mm});
            skLineSegment(sketch, "E284.3.0.3", {"start": v(-50.9, 146.5) * mm, "end": v(-50.9, 150.5) * mm});
            skLineSegment(sketch, "E284.3.0.4", {"start": v(-54.9, 150.5) * mm, "end": v(-50.9, 150.5) * mm});
            skLineSegment(sketch, "E284.direction1", {"start": v(12.4, 146.5) * mm, "end": v(-12.73, 146.5) * mm, "construction": true});
            skLineSegment(sketch, "E285.0.1.0", {"start": v(24.5, 127.87) * mm, "end": v(24.5, 114.87) * mm});
            skLineSegment(sketch, "E285.0.1.1", {"start": v(24.5, 123.87) * mm, "end": v(24.5, 127.87) * mm});
            skLineSegment(sketch, "E285.0.1.2", {"start": v(20.5, 127.87) * mm, "end": v(20.5, 114.87) * mm});
            skLineSegment(sketch, "E285.0.1.3", {"start": v(20.5, 114.87) * mm, "end": v(24.5, 114.87) * mm});
            skLineSegment(sketch, "E285.0.1.4", {"start": v(20.5, 127.87) * mm, "end": v(24.5, 127.87) * mm});
            skLineSegment(sketch, "E285.0.2.0", {"start": v(24.5, 105.25) * mm, "end": v(24.5, 92.25) * mm});
            skLineSegment(sketch, "E285.0.2.1", {"start": v(24.5, 101.25) * mm, "end": v(24.5, 105.25) * mm});
            skLineSegment(sketch, "E285.0.2.2", {"start": v(20.5, 105.25) * mm, "end": v(20.5, 92.25) * mm});
            skLineSegment(sketch, "E285.0.2.3", {"start": v(20.5, 92.25) * mm, "end": v(24.5, 92.25) * mm});
            skLineSegment(sketch, "E285.0.2.4", {"start": v(20.5, 105.25) * mm, "end": v(24.5, 105.25) * mm});
            skLineSegment(sketch, "E285.0.3.0", {"start": v(24.5, 82.62) * mm, "end": v(24.5, 69.62) * mm});
            skLineSegment(sketch, "E285.0.3.1", {"start": v(24.5, 78.62) * mm, "end": v(24.5, 82.62) * mm});
            skLineSegment(sketch, "E285.0.3.2", {"start": v(20.5, 82.62) * mm, "end": v(20.5, 69.62) * mm});
            skLineSegment(sketch, "E285.0.3.3", {"start": v(20.5, 69.62) * mm, "end": v(24.5, 69.62) * mm});
            skLineSegment(sketch, "E285.0.3.4", {"start": v(20.5, 82.62) * mm, "end": v(24.5, 82.62) * mm});
            skLineSegment(sketch, "E285.0.4.0", {"start": v(24.5, 47) * mm, "end": v(24.5, 60) * mm});
            skLineSegment(sketch, "E285.0.4.1", {"start": v(24.5, 56) * mm, "end": v(24.5, 60) * mm});
            skLineSegment(sketch, "E285.0.4.2", {"start": v(20.5, 60) * mm, "end": v(20.5, 47) * mm});
            skLineSegment(sketch, "E285.0.4.3", {"start": v(20.5, 47) * mm, "end": v(24.5, 47) * mm});
            skLineSegment(sketch, "E285.0.4.4", {"start": v(20.5, 60) * mm, "end": v(24.5, 60) * mm});
            skLineSegment(sketch, "E285.direction1", {"start": v(20.5, 137.5) * mm, "end": v(41, 137.5) * mm, "construction": true});
            skLineSegment(sketch, "E285.direction2", {"start": v(20.5, 137.5) * mm, "end": v(20.5, 114.87) * mm, "construction": true});
            skLineSegment(sketch, "E286.bottom", {"start": v(-59, 137.5) * mm, "end": v(-63, 137.5) * mm});
            skLineSegment(sketch, "E286.top", {"start": v(-59, 150.5) * mm, "end": v(-63, 150.5) * mm});
            skLineSegment(sketch, "E286.left", {"start": v(-59, 137.5) * mm, "end": v(-59, 150.5) * mm});
            skLineSegment(sketch, "E286.right", {"start": v(-63, 137.5) * mm, "end": v(-63, 150.5) * mm});
            skLineSegment(sketch, "E287.0.1.0", {"start": v(-59, 114.87) * mm, "end": v(-59, 127.87) * mm});
            skLineSegment(sketch, "E287.0.1.1", {"start": v(-63, 114.87) * mm, "end": v(-63, 127.87) * mm});
            skLineSegment(sketch, "E287.0.1.2", {"start": v(-59, 127.87) * mm, "end": v(-63, 127.87) * mm});
            skLineSegment(sketch, "E287.0.1.3", {"start": v(-59, 114.87) * mm, "end": v(-63, 114.87) * mm});
            skLineSegment(sketch, "E287.0.1.4", {"start": v(-63, 123.87) * mm, "end": v(-63, 127.87) * mm});
            skLineSegment(sketch, "E287.0.2.0", {"start": v(-59, 92.25) * mm, "end": v(-59, 105.25) * mm});
            skLineSegment(sketch, "E287.0.2.1", {"start": v(-63, 92.25) * mm, "end": v(-63, 105.25) * mm});
            skLineSegment(sketch, "E287.0.2.2", {"start": v(-59, 105.25) * mm, "end": v(-63, 105.25) * mm});
            skLineSegment(sketch, "E287.0.2.3", {"start": v(-59, 92.25) * mm, "end": v(-63, 92.25) * mm});
            skLineSegment(sketch, "E287.0.2.4", {"start": v(-63, 101.25) * mm, "end": v(-63, 105.25) * mm});
            skLineSegment(sketch, "E287.0.3.0", {"start": v(-59, 69.62) * mm, "end": v(-59, 82.62) * mm});
            skLineSegment(sketch, "E287.0.3.1", {"start": v(-63, 69.62) * mm, "end": v(-63, 82.62) * mm});
            skLineSegment(sketch, "E287.0.3.2", {"start": v(-59, 82.62) * mm, "end": v(-63, 82.62) * mm});
            skLineSegment(sketch, "E287.0.3.3", {"start": v(-59, 69.62) * mm, "end": v(-63, 69.62) * mm});
            skLineSegment(sketch, "E287.0.3.4", {"start": v(-63, 78.62) * mm, "end": v(-63, 82.62) * mm});
            skLineSegment(sketch, "E287.0.4.0", {"start": v(-59, 47) * mm, "end": v(-59, 60) * mm});
            skLineSegment(sketch, "E287.0.4.1", {"start": v(-63, 47) * mm, "end": v(-63, 60) * mm});
            skLineSegment(sketch, "E287.0.4.2", {"start": v(-59, 60) * mm, "end": v(-63, 60) * mm});
            skLineSegment(sketch, "E287.0.4.3", {"start": v(-59, 47) * mm, "end": v(-63, 47) * mm});
            skLineSegment(sketch, "E287.0.4.4", {"start": v(-63, 56) * mm, "end": v(-63, 60) * mm});
            skLineSegment(sketch, "E287.direction1", {"start": v(-63, 137.5) * mm, "end": v(-34, 137.5) * mm, "construction": true});
            skLineSegment(sketch, "E287.direction2", {"start": v(-63, 137.5) * mm, "end": v(-63, 114.87) * mm, "construction": true});
            skLineSegment(sketch, "E288.bottom", {"start": v(-63, 47) * mm, "end": v(-50.9, 47) * mm});
            skLineSegment(sketch, "E288.top", {"start": v(-63, 51) * mm, "end": v(-50.9, 51) * mm});
            skLineSegment(sketch, "E288.left", {"start": v(-63, 47) * mm, "end": v(-63, 51) * mm});
            skLineSegment(sketch, "E288.right", {"start": v(-50.9, 47) * mm, "end": v(-50.9, 51) * mm});
            skLineSegment(sketch, "E289.1.0.0", {"start": v(-37.87, 47) * mm, "end": v(-37.87, 51) * mm});
            skLineSegment(sketch, "E289.1.0.1", {"start": v(-37.87, 47) * mm, "end": v(-25.77, 47) * mm});
            skLineSegment(sketch, "E289.1.0.2", {"start": v(-25.77, 47) * mm, "end": v(-25.77, 51) * mm});
            skLineSegment(sketch, "E289.1.0.3", {"start": v(-37.87, 51) * mm, "end": v(-25.77, 51) * mm});
            skLineSegment(sketch, "E289.1.0.4", {"start": v(-33.87, 47) * mm, "end": v(-37.87, 47) * mm});
            skLineSegment(sketch, "E289.2.0.0", {"start": v(-12.73, 47) * mm, "end": v(-12.73, 51) * mm});
            skLineSegment(sketch, "E289.2.0.1", {"start": v(-12.73, 47) * mm, "end": v(-0.63, 47) * mm});
            skLineSegment(sketch, "E289.2.0.2", {"start": v(-0.63, 47) * mm, "end": v(-0.63, 51) * mm});
            skLineSegment(sketch, "E289.2.0.3", {"start": v(-12.73, 51) * mm, "end": v(-0.63, 51) * mm});
            skLineSegment(sketch, "E289.2.0.4", {"start": v(-8.73, 47) * mm, "end": v(-12.73, 47) * mm});
            skLineSegment(sketch, "E289.3.0.0", {"start": v(12.4, 47) * mm, "end": v(12.4, 51) * mm});
            skLineSegment(sketch, "E289.3.0.1", {"start": v(12.4, 47) * mm, "end": v(24.5, 47) * mm});
            skLineSegment(sketch, "E289.3.0.2", {"start": v(24.5, 47) * mm, "end": v(24.5, 51) * mm});
            skLineSegment(sketch, "E289.3.0.3", {"start": v(12.4, 51) * mm, "end": v(24.5, 51) * mm});
            skLineSegment(sketch, "E289.3.0.4", {"start": v(16.4, 47) * mm, "end": v(12.4, 47) * mm});
            skLineSegment(sketch, "E289.direction1", {"start": v(-63, 47) * mm, "end": v(-37.87, 47) * mm, "construction": true});
            skLineSegment(sketch, "E290", {"start": v(-19.25, 146.5) * mm, "end": v(-19.25, 125.62) * mm, "construction": true});
            skLineSegment(sketch, "E291.bottom", {"start": v(-32.5, 100.75) * mm, "end": v(-6, 100.75) * mm});
            skLineSegment(sketch, "E291.top", {"start": v(-32.5, 96.75) * mm, "end": v(-6, 96.75) * mm});
            skLineSegment(sketch, "E291.left", {"start": v(-32.5, 100.75) * mm, "end": v(-32.5, 96.75) * mm});
            skLineSegment(sketch, "E291.right", {"start": v(-6, 100.75) * mm, "end": v(-6, 96.75) * mm});
            skLineSegment(sketch, "E292.bottom", {"start": v(-32.5, 125.62) * mm, "end": v(-6, 125.62) * mm});
            skLineSegment(sketch, "E292.top", {"start": v(-32.5, 121.62) * mm, "end": v(-6, 121.62) * mm});
            skLineSegment(sketch, "E292.left", {"start": v(-32.5, 125.62) * mm, "end": v(-32.5, 121.62) * mm});
            skLineSegment(sketch, "E292.right", {"start": v(-6, 125.62) * mm, "end": v(-6, 121.62) * mm});
            skLineSegment(sketch, "E293", {"start": v(-32.5, 100.75) * mm, "end": v(-59, 100.75) * mm, "construction": true});
            skLineSegment(sketch, "E294", {"start": v(-6, 100.75) * mm, "end": v(20.5, 100.75) * mm, "construction": true});
            skLineSegment(sketch, "E295", {"start": v(-19.25, 121.62) * mm, "end": v(-19.25, 100.75) * mm, "construction": true});
            skLineSegment(sketch, "E296", {"start": v(-19.25, 96.75) * mm, "end": v(-19.25, 75.87) * mm, "construction": true});
            skLineSegment(sketch, "E297", {"start": v(-19.25, 71.87) * mm, "end": v(-19.25, 51) * mm, "construction": true});
            skLineSegment(sketch, "E298", {"start": v(-59, 75.87) * mm, "end": v(20.5, 75.87) * mm, "construction": true});
            skLineSegment(sketch, "E299", {"start": v(20.5, 71.87) * mm, "end": v(-59, 71.87) * mm, "construction": true});
            skSolve(sketch);
        }
        {
            var Q0;
            Q0 = qSketchRegion(id + "F17", true);
            extrude(context, id + "F18", {"entities" : qUnion([Q0]), "depth" : 4 * mm});
        }
        {
            var Q0;
            Q0=qCreatedBy(makeId("Front.planeOp"),FACE);
            var sketch = newSketch(context, id + "F19", { "sketchPlane" : qUnion([Q0])});
            skLineSegment(sketch, "E300", {"start": v(-63, 37) * mm, "end": v(-63, 25) * mm});
            skLineSegment(sketch, "E301", {"start": v(-63, 25) * mm, "end": v(-59, 25) * mm});
            skLineSegment(sketch, "E302", {"start": v(-59, 25) * mm, "end": v(-59, 16) * mm});
            skLineSegment(sketch, "E303", {"start": v(-59, 16) * mm, "end": v(-32.5, 16) * mm});
            skLineSegment(sketch, "E304", {"start": v(-32.5, 16) * mm, "end": v(-32.5, 12) * mm});
            skLineSegment(sketch, "E305", {"start": v(-32.5, 12) * mm, "end": v(-6, 12) * mm});
            skLineSegment(sketch, "E306", {"start": v(-6, 12) * mm, "end": v(-6, 16) * mm});
            skLineSegment(sketch, "E307", {"start": v(-6, 16) * mm, "end": v(20.5, 16) * mm});
            skLineSegment(sketch, "E308", {"start": v(20.5, 16) * mm, "end": v(20.5, 25) * mm});
            skLineSegment(sketch, "E309", {"start": v(20.5, 25) * mm, "end": v(24.5, 25) * mm});
            skLineSegment(sketch, "E310", {"start": v(24.5, 25) * mm, "end": v(24.5, 37) * mm});
            skLineSegment(sketch, "E311", {"start": v(24.5, 37) * mm, "end": v(20.5, 37) * mm});
            skLineSegment(sketch, "E312", {"start": v(20.5, 37) * mm, "end": v(20.5, 46) * mm});
            skLineSegment(sketch, "E313", {"start": v(20.5, 46) * mm, "end": v(-59, 46) * mm});
            skLineSegment(sketch, "E314", {"start": v(-59, 46) * mm, "end": v(-59, 37) * mm});
            skLineSegment(sketch, "E315", {"start": v(-59, 37) * mm, "end": v(-63, 37) * mm});
            skSolve(sketch);
        }
        {
            var Q0;
            Q0 = qSketchRegion(id + "F19", true);
            extrude(context, id + "F20", {"entities" : qUnion([Q0]), "depth" : 4 * mm});
        }
        {
            var Q0;
            Q0=qCreatedBy(makeId("Front.planeOp"),FACE);
            var sketch = newSketch(context, id + "F21", { "sketchPlane" : qUnion([Q0])});
            skLineSegment(sketch, "E316.bottom", {"start": v(20.5, 46) * mm, "end": v(-59, 46) * mm});
            skLineSegment(sketch, "E316.top", {"start": v(20.5, 16) * mm, "end": v(-59, 16) * mm});
            skLineSegment(sketch, "E316.left", {"start": v(20.5, 46) * mm, "end": v(20.5, 16) * mm});
            skLineSegment(sketch, "E316.right", {"start": v(-59, 46) * mm, "end": v(-59, 16) * mm});
            skLineSegment(sketch, "E317.bottom", {"start": v(24.5, 37) * mm, "end": v(20.5, 37) * mm});
            skLineSegment(sketch, "E317.top", {"start": v(24.5, 25) * mm, "end": v(20.5, 25) * mm});
            skLineSegment(sketch, "E317.left", {"start": v(24.5, 37) * mm, "end": v(24.5, 25) * mm});
            skLineSegment(sketch, "E317.right", {"start": v(20.5, 37) * mm, "end": v(20.5, 25) * mm});
            skLineSegment(sketch, "E318.bottom", {"start": v(-63, 37) * mm, "end": v(-59, 37) * mm});
            skLineSegment(sketch, "E318.top", {"start": v(-63, 25) * mm, "end": v(-59, 25) * mm});
            skLineSegment(sketch, "E318.left", {"start": v(-63, 37) * mm, "end": v(-63, 25) * mm});
            skLineSegment(sketch, "E318.right", {"start": v(-59, 37) * mm, "end": v(-59, 25) * mm});
            skLineSegment(sketch, "E319.bottom", {"start": v(12.4, 12) * mm, "end": v(-0.63, 12) * mm});
            skLineSegment(sketch, "E319.top", {"start": v(12.4, 16) * mm, "end": v(-0.63, 16) * mm});
            skLineSegment(sketch, "E319.left", {"start": v(12.4, 12) * mm, "end": v(12.4, 16) * mm});
            skLineSegment(sketch, "E319.right", {"start": v(-0.63, 12) * mm, "end": v(-0.63, 16) * mm});
            skLineSegment(sketch, "E320.bottom", {"start": v(-12.73, 16) * mm, "end": v(-25.77, 16) * mm});
            skLineSegment(sketch, "E320.top", {"start": v(-12.73, 12) * mm, "end": v(-25.77, 12) * mm});
            skLineSegment(sketch, "E320.left", {"start": v(-12.73, 16) * mm, "end": v(-12.73, 12) * mm});
            skLineSegment(sketch, "E320.right", {"start": v(-25.77, 16) * mm, "end": v(-25.77, 12) * mm});
            skLineSegment(sketch, "E321.bottom", {"start": v(-37.87, 12) * mm, "end": v(-50.9, 12) * mm});
            skLineSegment(sketch, "E321.top", {"start": v(-37.87, 16) * mm, "end": v(-50.9, 16) * mm});
            skLineSegment(sketch, "E321.left", {"start": v(-37.87, 12) * mm, "end": v(-37.87, 16) * mm});
            skLineSegment(sketch, "E321.right", {"start": v(-50.9, 12) * mm, "end": v(-50.9, 16) * mm});
            skSolve(sketch);
        }
        {
            var Q0;
            Q0 = qSketchRegion(id + "F21", true);
            extrude(context, id + "F22", {"entities" : qUnion([Q0]), "oppositeDirection" : true, "depth" : 4 * mm});
        }
        {
            var Q0;
            Q0=qCreatedBy(makeId("Right.planeOp"),FACE);
            var sketch = newSketch(context, id + "F23", { "sketchPlane" : qUnion([Q0])});
            skLineSegment(sketch, "E322.bottom", {"start": v(150.5, 46) * mm, "end": v(75.87, 46) * mm});
            skLineSegment(sketch, "E322.top", {"start": v(150.5, 16) * mm, "end": v(47, 16) * mm});
            skLineSegment(sketch, "E322.left", {"start": v(150.5, 46) * mm, "end": v(150.5, 37) * mm});
            skLineSegment(sketch, "E322.right", {"start": v(47, 46) * mm, "end": v(47, 37) * mm});
            skLineSegment(sketch, "E323", {"start": v(47, 37) * mm, "end": v(51, 37) * mm});
            skLineSegment(sketch, "E324", {"start": v(51, 37) * mm, "end": v(51, 25) * mm});
            skLineSegment(sketch, "E325", {"start": v(51, 25) * mm, "end": v(47, 25) * mm});
            skLineSegment(sketch, "E326", {"start": v(150.5, 25) * mm, "end": v(146.5, 25) * mm});
            skLineSegment(sketch, "E327", {"start": v(146.5, 25) * mm, "end": v(146.5, 37) * mm});
            skLineSegment(sketch, "E328", {"start": v(146.5, 37) * mm, "end": v(150.5, 37) * mm});
            skLineSegment(sketch, "E329.trimOffspring", {"start": v(150.5, 25) * mm, "end": v(150.5, 16) * mm});
            skLineSegment(sketch, "E330.trimOffspring", {"start": v(47, 25) * mm, "end": v(47, 16) * mm});
            skLineSegment(sketch, "E331.left", {"start": v(137.5, 16) * mm, "end": v(137.5, 12) * mm});
            skLineSegment(sketch, "E331.right", {"start": v(127.87, 16) * mm, "end": v(127.87, 12) * mm});
            skLineSegment(sketch, "E332.bottom", {"start": v(114.87, 16) * mm, "end": v(105.25, 16) * mm});
            skLineSegment(sketch, "E332.left", {"start": v(114.87, 16) * mm, "end": v(114.87, 12) * mm});
            skLineSegment(sketch, "E332.right", {"start": v(105.25, 16) * mm, "end": v(105.25, 12) * mm});
            skLineSegment(sketch, "E333.bottom", {"start": v(92.25, 16) * mm, "end": v(82.62, 16) * mm});
            skLineSegment(sketch, "E333.left", {"start": v(92.25, 16) * mm, "end": v(92.25, 12) * mm});
            skLineSegment(sketch, "E333.right", {"start": v(82.62, 16) * mm, "end": v(82.62, 12) * mm});
            skLineSegment(sketch, "E334.bottom", {"start": v(69.62, 16) * mm, "end": v(60, 16) * mm});
            skLineSegment(sketch, "E334.left", {"start": v(69.62, 16) * mm, "end": v(69.62, 12) * mm});
            skLineSegment(sketch, "E334.right", {"start": v(60, 16) * mm, "end": v(60, 12) * mm});
            skLineSegment(sketch, "E335.bottom", {"start": v(125.62, 37) * mm, "end": v(121.62, 37) * mm});
            skLineSegment(sketch, "E335.top", {"start": v(125.62, 25) * mm, "end": v(121.62, 25) * mm});
            skLineSegment(sketch, "E335.left", {"start": v(125.62, 37) * mm, "end": v(125.62, 25) * mm});
            skLineSegment(sketch, "E335.right", {"start": v(121.62, 37) * mm, "end": v(121.62, 25) * mm});
            skLineSegment(sketch, "E336.bottom", {"start": v(100.75, 37) * mm, "end": v(96.75, 37) * mm});
            skLineSegment(sketch, "E336.top", {"start": v(100.75, 25) * mm, "end": v(96.75, 25) * mm});
            skLineSegment(sketch, "E336.left", {"start": v(100.75, 37) * mm, "end": v(100.75, 25) * mm});
            skLineSegment(sketch, "E336.right", {"start": v(96.75, 37) * mm, "end": v(96.75, 25) * mm});
            skLineSegment(sketch, "E337", {"start": v(71.87, 46) * mm, "end": v(71.87, 37) * mm});
            skLineSegment(sketch, "E338", {"start": v(71.87, 37) * mm, "end": v(75.87, 37) * mm});
            skLineSegment(sketch, "E339", {"start": v(75.87, 37) * mm, "end": v(75.87, 46) * mm});
            skLineSegment(sketch, "E340.trimOffspring", {"start": v(71.87, 46) * mm, "end": v(47, 46) * mm});
            skLineSegment(sketch, "E341", {"start": v(60, 12) * mm, "end": v(69.62, 12) * mm});
            skLineSegment(sketch, "E342", {"start": v(82.62, 12) * mm, "end": v(92.25, 12) * mm});
            skLineSegment(sketch, "E343", {"start": v(105.25, 12) * mm, "end": v(114.87, 12) * mm});
            skLineSegment(sketch, "E344", {"start": v(127.87, 12) * mm, "end": v(137.5, 12) * mm});
            skSolve(sketch);
        }
        {
            var Q0;
            Q0 = qSketchRegion(id + "F23", true);
            extrude(context, id + "F24", {"entities" : qUnion([Q0]), "depth" : 4 * mm});
        }
        {
            var Q0;
            Q0=qCreatedBy(makeId("Front.planeOp"),FACE);
            var sketch = newSketch(context, id + "F25", { "sketchPlane" : qUnion([Q0])});
            skLineSegment(sketch, "E345", {"start": v(-63, 46) * mm, "end": v(-63, 37) * mm});
            skLineSegment(sketch, "E346", {"start": v(-63, 37) * mm, "end": v(-59, 37) * mm});
            skLineSegment(sketch, "E347", {"start": v(-59, 37) * mm, "end": v(-59, 16) * mm});
            skLineSegment(sketch, "E348", {"start": v(-59, 16) * mm, "end": v(20.5, 16) * mm});
            skLineSegment(sketch, "E349", {"start": v(20.5, 16) * mm, "end": v(20.5, 37) * mm});
            skLineSegment(sketch, "E350", {"start": v(20.5, 37) * mm, "end": v(24.5, 37) * mm});
            skLineSegment(sketch, "E351", {"start": v(24.5, 37) * mm, "end": v(24.5, 46) * mm});
            skLineSegment(sketch, "E352", {"start": v(24.5, 46) * mm, "end": v(-63, 46) * mm});
            skSolve(sketch);
        }
        {
            var Q0;
            Q0 = qSketchRegion(id + "F25", true);
            extrude(context, id + "F26", {"entities" : qUnion([Q0]), "depth" : 4 * mm});
        }
        {
            var Q0;
            Q0=qCreatedBy(makeId("Right.planeOp"),FACE);
            var sketch = newSketch(context, id + "F27", { "sketchPlane" : qUnion([Q0])});
            skLineSegment(sketch, "E353", {"start": v(14, 46) * mm, "end": v(-57, 46) * mm});
            skLineSegment(sketch, "E354", {"start": v(-57, 46) * mm, "end": v(-57, 34) * mm});
            skLineSegment(sketch, "E355", {"start": v(-57, 34) * mm, "end": v(-151, 34) * mm});
            skLineSegment(sketch, "E356", {"start": v(-151, 34) * mm, "end": v(-151, 4) * mm});
            skLineSegment(sketch, "E357", {"start": v(-151, 4) * mm, "end": v(-123.5, 4) * mm});
            skLineSegment(sketch, "E358", {"start": v(14, 4) * mm, "end": v(14, 46) * mm});
            skLineSegment(sketch, "E359.bottom", {"start": v(-123.5, 19) * mm, "end": v(-119.5, 19) * mm});
            skLineSegment(sketch, "E359.left", {"start": v(-123.5, 19) * mm, "end": v(-123.5, 4) * mm});
            skLineSegment(sketch, "E359.right", {"start": v(-119.5, 19) * mm, "end": v(-119.5, 4) * mm});
            skLineSegment(sketch, "E360.bottom", {"start": v(-86, 19) * mm, "end": v(-82, 19) * mm});
            skLineSegment(sketch, "E360.left", {"start": v(-86, 19) * mm, "end": v(-86, 4) * mm});
            skLineSegment(sketch, "E360.right", {"start": v(-82, 19) * mm, "end": v(-82, 4) * mm});
            skLineSegment(sketch, "E361.bottom", {"start": v(-48.5, 25) * mm, "end": v(-44.5, 25) * mm});
            skLineSegment(sketch, "E361.left", {"start": v(-48.5, 25) * mm, "end": v(-48.5, 4) * mm});
            skLineSegment(sketch, "E361.right", {"start": v(-44.5, 25) * mm, "end": v(-44.5, 4) * mm});
            skLineSegment(sketch, "E362", {"start": v(-151, 19) * mm, "end": v(-123.5, 19) * mm, "construction": true});
            skLineSegment(sketch, "E363", {"start": v(-119.5, 19) * mm, "end": v(-86, 19) * mm, "construction": true});
            skLineSegment(sketch, "E364", {"start": v(-82, 19) * mm, "end": v(-48.5, 19) * mm, "construction": true});
            skLineSegment(sketch, "E365", {"start": v(-82, 19) * mm, "end": v(-82, 34) * mm, "construction": true});
            skLineSegment(sketch, "E366", {"start": v(-44.5, 25) * mm, "end": v(-44.5, 46) * mm, "construction": true});
            skLineSegment(sketch, "E367.trimOffspring", {"start": v(-119.5, 4) * mm, "end": v(-86, 4) * mm});
            skLineSegment(sketch, "E368.trimOffspring", {"start": v(-82, 4) * mm, "end": v(-48.5, 4) * mm});
            skLineSegment(sketch, "E369.trimOffspring", {"start": v(-44.5, 4) * mm, "end": v(14, 4) * mm});
            skSolve(sketch);
        }
        {
            var Q0;
            Q0 = qSketchRegion(id + "F27", true);
            extrude(context, id + "F28", {"entities" : qUnion([Q0]), "oppositeDirection" : true, "depth" : (getVariable(context, 'thickness')) * mm});
        }
        {
            var Q0;
            Q0=qCreatedBy(makeId("Front.planeOp"),FACE);
            var sketch = newSketch(context, id + "F29", { "sketchPlane" : qUnion([Q0])});
            skLineSegment(sketch, "E370", {"start": v(-67, 46) * mm, "end": v(-55, 46) * mm});
            skLineSegment(sketch, "E371", {"start": v(-51, 42) * mm, "end": v(-51, 34) * mm});
            skLineSegment(sketch, "E372", {"start": v(-51, 34) * mm, "end": v(-21, 34) * mm});
            skLineSegment(sketch, "E373", {"start": v(13, 34) * mm, "end": v(13, 42) * mm});
            skLineSegment(sketch, "E374", {"start": v(17, 46) * mm, "end": v(29, 46) * mm});
            skLineSegment(sketch, "E375", {"start": v(29, 46) * mm, "end": v(29, 34) * mm});
            skLineSegment(sketch, "E376", {"start": v(25, 34) * mm, "end": v(25, 4) * mm});
            skLineSegment(sketch, "E377", {"start": v(25, 4) * mm, "end": v(-63, 4) * mm});
            skLineSegment(sketch, "E378", {"start": v(-63, 4) * mm, "end": v(-63, 34) * mm});
            skLineSegment(sketch, "E379", {"start": v(-63, 34) * mm, "end": v(-67, 34) * mm});
            skLineSegment(sketch, "E380", {"start": v(-67, 34) * mm, "end": v(-67, 46) * mm});
            skLineSegment(sketch, "E381", {"start": v(29, 34) * mm, "end": v(25, 34) * mm});
            skLineSegment(sketch, "E382", {"start": v(-63, 34) * mm, "end": v(-51, 34) * mm, "construction": true});
            skLineSegment(sketch, "E383", {"start": v(25, 34) * mm, "end": v(13, 34) * mm, "construction": true});
            skLineSegment(sketch, "E384.top", {"start": v(-21, 19) * mm, "end": v(-17, 19) * mm});
            skLineSegment(sketch, "E384.left", {"start": v(-21, 34) * mm, "end": v(-21, 19) * mm});
            skLineSegment(sketch, "E384.right", {"start": v(-17, 34) * mm, "end": v(-17, 19) * mm});
            skLineSegment(sketch, "E385.trimOffspring", {"start": v(-17, 34) * mm, "end": v(13, 34) * mm});
            skPoint(sketch, "E386.visualSharp", {"position": v(-51, 46) * mm});
            skArc(sketch, "E386.filletArc", {"start": v(-51, 42) * mm, "mid": v(-52.17, 44.83) * mm, "end": v(-55, 46) * mm});
            skPoint(sketch, "E387.visualSharp", {"position": v(13, 46) * mm});
            skArc(sketch, "E387.filletArc", {"start": v(17, 46) * mm, "mid": v(14.17, 44.83) * mm, "end": v(13, 42) * mm});
            skSolve(sketch);
        }
        {
            var Q0;
            Q0 = qSketchRegion(id + "F29", true);
            extrude(context, id + "F30", {"entities" : qUnion([Q0]), "depth" : (getVariable(context, 'thickness')) * mm});
        }
        {
            var Q0;
            Q0=qCreatedBy(makeId("Front.planeOp"),FACE);
            var sketch = newSketch(context, id + "F31", { "sketchPlane" : qUnion([Q0])});
            skLineSegment(sketch, "E388", {"start": v(-67, 46) * mm, "end": v(-67, 34) * mm});
            skLineSegment(sketch, "E389", {"start": v(-67, 34) * mm, "end": v(-63, 34) * mm});
            skLineSegment(sketch, "E390", {"start": v(-63, 34) * mm, "end": v(-63, 4) * mm});
            skLineSegment(sketch, "E391", {"start": v(-63, 4) * mm, "end": v(25, 4) * mm});
            skLineSegment(sketch, "E392", {"start": v(25, 4) * mm, "end": v(25, 34) * mm});
            skLineSegment(sketch, "E393", {"start": v(25, 34) * mm, "end": v(29, 34) * mm});
            skLineSegment(sketch, "E394", {"start": v(29, 34) * mm, "end": v(29, 46) * mm});
            skLineSegment(sketch, "E395", {"start": v(29, 46) * mm, "end": v(-17, 46) * mm});
            skLineSegment(sketch, "E396.top", {"start": v(-21, 25) * mm, "end": v(-17, 25) * mm});
            skLineSegment(sketch, "E396.left", {"start": v(-21, 46) * mm, "end": v(-21, 25) * mm});
            skLineSegment(sketch, "E396.right", {"start": v(-17, 46) * mm, "end": v(-17, 25) * mm});
            skLineSegment(sketch, "E397.trimOffspring", {"start": v(-21, 46) * mm, "end": v(-67, 46) * mm});
            skSolve(sketch);
        }
        {
            var Q0;
            Q0 = qSketchRegion(id + "F31", true);
            extrude(context, id + "F32", {"entities" : qUnion([Q0]), "oppositeDirection" : true, "depth" : (getVariable(context, 'thickness')) * mm});
        }
        {
            var Q0;
            Q0=qCreatedBy(makeId("Front.planeOp"),FACE);
            var sketch = newSketch(context, id + "F33", { "sketchPlane" : qUnion([Q0])});
            skLineSegment(sketch, "E398", {"start": v(25, 46) * mm, "end": v(25, 34) * mm});
            skLineSegment(sketch, "E399", {"start": v(25, 34) * mm, "end": v(29, 34) * mm});
            skLineSegment(sketch, "E400", {"start": v(29, 34) * mm, "end": v(29, 4) * mm});
            skLineSegment(sketch, "E401", {"start": v(29, 4) * mm, "end": v(106, 4) * mm});
            skLineSegment(sketch, "E402", {"start": v(106, 4) * mm, "end": v(106, 34) * mm});
            skLineSegment(sketch, "E403", {"start": v(106, 34) * mm, "end": v(110, 34) * mm});
            skLineSegment(sketch, "E404", {"start": v(110, 34) * mm, "end": v(110, 46) * mm});
            skLineSegment(sketch, "E405", {"start": v(110, 46) * mm, "end": v(94.2, 46) * mm});
            skLineSegment(sketch, "E406", {"start": v(25, 46) * mm, "end": v(40.8, 46) * mm});
            skArc(sketch, "E407", {"start": v(44.75, 42.6) * mm, "mid": v(67.5, 23) * mm, "end": v(90.25, 42.6) * mm});
            skPoint(sketch, "E408.visualSharp", {"position": v(44.5, 46) * mm});
            skArc(sketch, "E408.filletArc", {"start": v(44.75, 42.6) * mm, "mid": v(43.4, 45.03) * mm, "end": v(40.8, 46) * mm});
            skPoint(sketch, "E409.visualSharp", {"position": v(90.5, 46) * mm});
            skArc(sketch, "E409.filletArc", {"start": v(94.2, 46) * mm, "mid": v(91.6, 45.03) * mm, "end": v(90.25, 42.6) * mm});
            skSolve(sketch);
        }
        {
            var Q0;
            Q0 = qSketchRegion(id + "F33", true);
            extrude(context, id + "F34", {"entities" : qUnion([Q0]), "depth" : (getVariable(context, 'thickness')) * mm});
        }
        {
            var Q0;
            Q0=qCreatedBy(makeId("Front.planeOp"),FACE);
            var sketch = newSketch(context, id + "F35", { "sketchPlane" : qUnion([Q0])});
            skLineSegment(sketch, "E410", {"start": v(-110, 46) * mm, "end": v(-110, 34) * mm});
            skLineSegment(sketch, "E411", {"start": v(-110, 34) * mm, "end": v(-106, 34) * mm});
            skLineSegment(sketch, "E412", {"start": v(-106, 34) * mm, "end": v(-106, 4) * mm});
            skLineSegment(sketch, "E413", {"start": v(-106, 4) * mm, "end": v(-67, 4) * mm});
            skLineSegment(sketch, "E414", {"start": v(-67, 4) * mm, "end": v(-67, 34) * mm});
            skLineSegment(sketch, "E415", {"start": v(-67, 34) * mm, "end": v(-63, 34) * mm});
            skLineSegment(sketch, "E416", {"start": v(-63, 34) * mm, "end": v(-63, 46) * mm});
            skLineSegment(sketch, "E417", {"start": v(-63, 46) * mm, "end": v(-71.5, 46) * mm});
            skLineSegment(sketch, "E418", {"start": v(-75.5, 42) * mm, "end": v(-75.5, 34) * mm});
            skLineSegment(sketch, "E419", {"start": v(-110, 46) * mm, "end": v(-101.5, 46) * mm});
            skLineSegment(sketch, "E420", {"start": v(-97.5, 42) * mm, "end": v(-97.5, 34) * mm});
            skArc(sketch, "E421", {"start": v(-97.5, 34) * mm, "mid": v(-86.5, 23) * mm, "end": v(-75.5, 34) * mm});
            skLineSegment(sketch, "E422", {"start": v(-75.5, 34) * mm, "end": v(-97.5, 34) * mm, "construction": true});
            skPoint(sketch, "E423.visualSharp", {"position": v(-75.5, 46) * mm});
            skArc(sketch, "E423.filletArc", {"start": v(-71.5, 46) * mm, "mid": v(-74.33, 44.83) * mm, "end": v(-75.5, 42) * mm});
            skPoint(sketch, "E424.visualSharp", {"position": v(-97.5, 46) * mm});
            skArc(sketch, "E424.filletArc", {"start": v(-97.5, 42) * mm, "mid": v(-98.67, 44.83) * mm, "end": v(-101.5, 46) * mm});
            skSolve(sketch);
        }
        {
            var Q0;
            Q0 = qSketchRegion(id + "F35", true);
            extrude(context, id + "F36", {"entities" : qUnion([Q0]), "depth" : (getVariable(context, 'thickness')) * mm});
        }
    });
